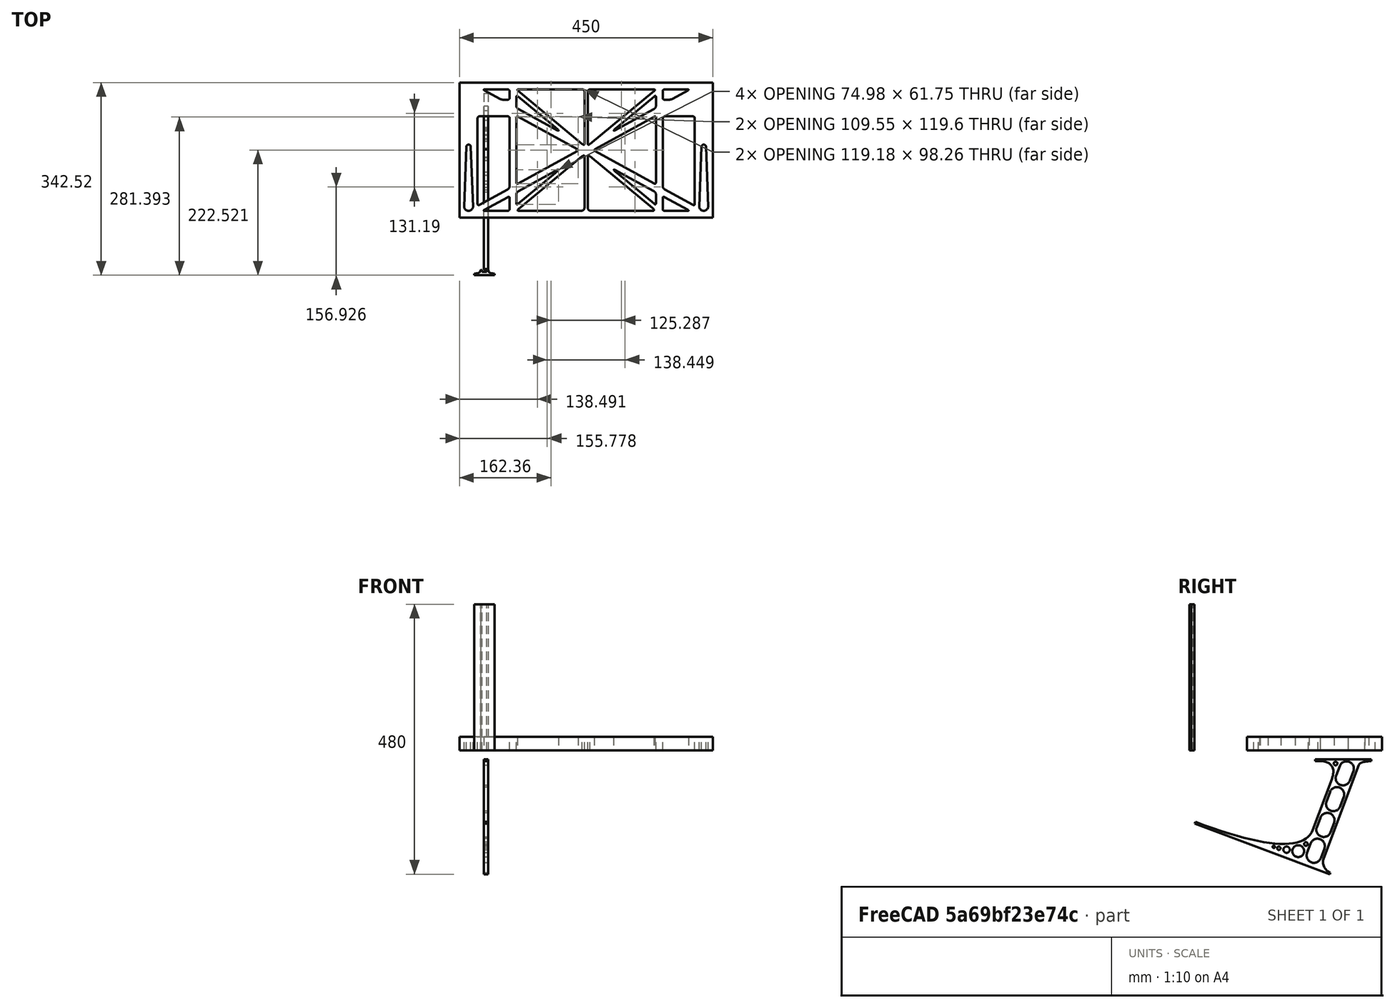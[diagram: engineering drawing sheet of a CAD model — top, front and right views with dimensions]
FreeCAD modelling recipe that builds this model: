
FCSTD DOCUMENT  (FreeCAD 0.19R0.19.2)
Label: laptopStand163FCStd
License: All rights reserved
LicenseURL: http://en.wikipedia.org/wiki/All_rights_reserved
objects: Sketcher::SketchObject×4, Part::Extrusion×3
note: 7 computed .brp shape members not serialized (recipe doc carries the construction recipe); baked Part::Feature solids carry a one-line shape summary decoded from their .brp

FEATURE [Sketcher::SketchObject] Sketch
  FullyConstrained = false
  sketch-geometry (349):
    g0: LineSegment StartX=-10.9272 StartY=-82.7794 StartZ=0 EndX=46.0728 EndY=-51.4823 EndZ=0
    g1: LineSegment StartX=-10.9272 StartY=76.4095 StartZ=0 EndX=-10.9272 EndY=-82.7794 EndZ=0
    g2: LineSegment StartX=46.0728 StartY=76.4095 StartZ=0 EndX=46.0728 EndY=-51.4823 EndZ=0
    g3: LineSegment StartX=-42.9272 StartY=136.221 StartZ=0 EndX=-42.9272 EndY=-103.779 EndZ=0
    g4: LineSegment StartX=407.073 StartY=136.221 StartZ=0 EndX=407.073 EndY=-103.779 EndZ=0
    g5: ArcOfCircle CenterX=-26.9272 CenterY=-83.7794 CenterZ=0 NormalX=0 NormalY=0 NormalZ=1 AngleXU=0 Radius=8 StartAngle=3.14159 EndAngle=6.28319
    g6: ArcOfCircle CenterX=391.073 CenterY=22.1087 CenterZ=0 NormalX=0 NormalY=0 NormalZ=1 AngleXU=0 Radius=8 StartAngle=-4.4e-15 EndAngle=3.14159
    g7: LineSegment StartX=399.073 StartY=22.1087 StartZ=0 EndX=399.073 EndY=-83.7794 EndZ=0
    g8: LineSegment StartX=383.073 StartY=22.1087 StartZ=0 EndX=383.073 EndY=-83.7794 EndZ=0
    g9: ArcOfCircle CenterX=391.073 CenterY=-83.7794 CenterZ=0 NormalX=0 NormalY=0 NormalZ=1 AngleXU=0 Radius=8 StartAngle=3.14159 EndAngle=6.28319
    g10: Circle CenterX=175.022 CenterY=27.0628 CenterZ=0 NormalX=0 NormalY=0 NormalZ=1 AngleXU=0 Radius=1
    g11: Circle CenterX=179.022 CenterY=24.8665 CenterZ=0 NormalX=0 NormalY=0 NormalZ=1 AngleXU=0 Radius=1
    g12: Circle CenterX=179.022 CenterY=27.0628 CenterZ=0 NormalX=0 NormalY=0 NormalZ=1 AngleXU=0 Radius=1
    g13: BSplineCurve PolesCount=3 KnotsCount=2 Degree=2 IsPeriodic=0
    g14: GeomPoint X=175.022 Y=27.0628 Z=0
    g15: GeomPoint X=179.022 Y=27.0628 Z=0
    g16: Circle CenterX=189.124 CenterY=27.0628 CenterZ=0 NormalX=0 NormalY=0 NormalZ=1 AngleXU=0 Radius=1
    g17: Circle CenterX=185.124 CenterY=24.8665 CenterZ=0 NormalX=0 NormalY=0 NormalZ=1 AngleXU=0 Radius=1
    g18: Circle CenterX=185.124 CenterY=27.0628 CenterZ=0 NormalX=0 NormalY=0 NormalZ=1 AngleXU=0 Radius=1
    g19: BSplineCurve PolesCount=3 KnotsCount=2 Degree=2 IsPeriodic=0
    g20: GeomPoint X=189.124 Y=27.0628 Z=0
    g21: GeomPoint X=185.124 Y=27.0628 Z=0
    g22: Circle CenterX=175.022 CenterY=5.37834 CenterZ=0 NormalX=0 NormalY=0 NormalZ=1 AngleXU=0 Radius=1
    g23: Circle CenterX=179.022 CenterY=7.57463 CenterZ=0 NormalX=0 NormalY=0 NormalZ=1 AngleXU=0 Radius=1
    g24: Circle CenterX=179.022 CenterY=5.34704 CenterZ=0 NormalX=0 NormalY=0 NormalZ=1 AngleXU=0 Radius=1
    g25: BSplineCurve PolesCount=3 KnotsCount=2 Degree=2 IsPeriodic=0
    g26: GeomPoint X=175.022 Y=5.37834 Z=0
    g27: GeomPoint X=179.022 Y=5.34704 Z=0
    g28: Circle CenterX=189.124 CenterY=5.37834 CenterZ=0 NormalX=0 NormalY=0 NormalZ=1 AngleXU=0 Radius=1
    g29: Circle CenterX=185.124 CenterY=7.57463 CenterZ=0 NormalX=0 NormalY=0 NormalZ=1 AngleXU=0 Radius=1
    g30: Circle CenterX=185.124 CenterY=5.34704 CenterZ=0 NormalX=0 NormalY=0 NormalZ=1 AngleXU=0 Radius=1
    g31: BSplineCurve PolesCount=3 KnotsCount=2 Degree=2 IsPeriodic=0
    g32: GeomPoint X=189.124 Y=5.37834 Z=0
    g33: GeomPoint X=185.124 Y=5.34704 Z=0
    g34: Circle CenterX=165.871 CenterY=18.1458 CenterZ=0 NormalX=0 NormalY=0 NormalZ=1 AngleXU=0 Radius=1
    g35: Circle CenterX=169.377 CenterY=16.2206 CenterZ=0 NormalX=0 NormalY=0 NormalZ=1 AngleXU=0 Radius=1
    g36: Circle CenterX=165.871 CenterY=14.2954 CenterZ=0 NormalX=0 NormalY=0 NormalZ=1 AngleXU=0 Radius=1
    g37: BSplineCurve PolesCount=3 KnotsCount=2 Degree=2 IsPeriodic=0
    g38: GeomPoint X=165.871 Y=18.1458 Z=0
    g39: GeomPoint X=165.871 Y=14.2954 Z=0
    g40: Circle CenterX=198.275 CenterY=18.1458 CenterZ=0 NormalX=0 NormalY=0 NormalZ=1 AngleXU=0 Radius=1
    g41: Circle CenterX=194.768 CenterY=16.2206 CenterZ=0 NormalX=0 NormalY=0 NormalZ=1 AngleXU=0 Radius=1
    g42: Circle CenterX=198.275 CenterY=14.2954 CenterZ=0 NormalX=0 NormalY=0 NormalZ=1 AngleXU=0 Radius=1
    g43: BSplineCurve PolesCount=3 KnotsCount=2 Degree=2 IsPeriodic=0
    g44: GeomPoint X=198.275 Y=18.1458 Z=0
    g45: GeomPoint X=198.275 Y=14.2954 Z=0
    g46: LineSegment StartX=407.073 StartY=-103.779 StartZ=0 EndX=-42.9272 EndY=-103.779 EndZ=0
    g47: LineSegment StartX=407.073 StartY=136.221 StartZ=0 EndX=-42.9272 EndY=136.221 EndZ=0
    g48: LineSegment StartX=46.0728 StartY=76.4095 StartZ=0 EndX=-10.9272 EndY=76.4095 EndZ=0
    g49: Circle CenterX=125.607 CenterY=54.1951 CenterZ=0 NormalX=0 NormalY=0 NormalZ=1 AngleXU=0 Radius=1
    g50: Circle CenterX=139.632 CenterY=46.4944 CenterZ=0 NormalX=0 NormalY=0 NormalZ=1 AngleXU=0 Radius=1
    g51: Circle CenterX=127.326 CenterY=56.7187 CenterZ=0 NormalX=0 NormalY=0 NormalZ=1 AngleXU=0 Radius=1
    g52: BSplineCurve PolesCount=3 KnotsCount=2 Degree=2 IsPeriodic=0
    g53: GeomPoint X=125.607 Y=54.1951 Z=0
    g54: GeomPoint X=127.326 Y=56.7187 Z=0
    g55: Circle CenterX=236.821 CenterY=56.7187 CenterZ=0 NormalX=0 NormalY=0 NormalZ=1 AngleXU=0 Radius=1
    g56: Circle CenterX=224.513 CenterY=46.4944 CenterZ=0 NormalX=0 NormalY=0 NormalZ=1 AngleXU=0 Radius=1
    g57: Circle CenterX=238.538 CenterY=54.1951 CenterZ=0 NormalX=0 NormalY=0 NormalZ=1 AngleXU=0 Radius=1
    g58: BSplineCurve PolesCount=3 KnotsCount=2 Degree=2 IsPeriodic=0
    g59: GeomPoint X=236.821 Y=56.7187 Z=0
    g60: GeomPoint X=238.538 Y=54.1951 Z=0
    g61: Circle CenterX=238.538 CenterY=-21.7539 CenterZ=0 NormalX=0 NormalY=0 NormalZ=1 AngleXU=0 Radius=1
    g62: Circle CenterX=224.513 CenterY=-14.0532 CenterZ=0 NormalX=0 NormalY=0 NormalZ=1 AngleXU=0 Radius=1
    g63: Circle CenterX=236.821 CenterY=-24.2775 CenterZ=0 NormalX=0 NormalY=0 NormalZ=1 AngleXU=0 Radius=1
    g64: BSplineCurve PolesCount=3 KnotsCount=2 Degree=2 IsPeriodic=0
    g65: GeomPoint X=238.538 Y=-21.7539 Z=0
    g66: GeomPoint X=236.821 Y=-24.2775 Z=0
    g67: Circle CenterX=125.607 CenterY=-21.7539 CenterZ=0 NormalX=0 NormalY=0 NormalZ=1 AngleXU=0 Radius=1
    g68: Circle CenterX=139.632 CenterY=-14.0532 CenterZ=0 NormalX=0 NormalY=0 NormalZ=1 AngleXU=0 Radius=1
    g69: Circle CenterX=127.325 CenterY=-24.2775 CenterZ=0 NormalX=0 NormalY=0 NormalZ=1 AngleXU=0 Radius=1
    g70: BSplineCurve PolesCount=3 KnotsCount=2 Degree=2 IsPeriodic=0
    g71: GeomPoint X=125.607 Y=-21.7539 Z=0
    g72: GeomPoint X=127.325 Y=-24.2775 Z=0
    g73: Circle CenterX=302.996 CenterY=111.695 CenterZ=0 NormalX=0 NormalY=0 NormalZ=1 AngleXU=0 Radius=1
    g74: Circle CenterX=306.073 CenterY=114.251 CenterZ=0 NormalX=0 NormalY=0 NormalZ=1 AngleXU=0 Radius=1
    g75: Circle CenterX=306.073 CenterY=110.251 CenterZ=0 NormalX=0 NormalY=0 NormalZ=1 AngleXU=0 Radius=1
    g76: BSplineCurve PolesCount=3 KnotsCount=2 Degree=2 IsPeriodic=0
    g77: GeomPoint X=302.996 Y=111.695 Z=0
    g78: GeomPoint X=306.073 Y=110.251 Z=0
    g79: Circle CenterX=306.073 CenterY=95.2763 CenterZ=0 NormalX=0 NormalY=0 NormalZ=1 AngleXU=0 Radius=1
    g80: Circle CenterX=306.073 CenterY=91.2763 CenterZ=0 NormalX=0 NormalY=0 NormalZ=1 AngleXU=0 Radius=1
    g81: Circle CenterX=302.567 CenterY=89.3511 CenterZ=0 NormalX=0 NormalY=0 NormalZ=1 AngleXU=0 Radius=1
    g82: BSplineCurve PolesCount=3 KnotsCount=2 Degree=2 IsPeriodic=0
    g83: GeomPoint X=306.073 Y=95.2763 Z=0
    g84: GeomPoint X=302.567 Y=89.3511 Z=0
    g85: LineSegment StartX=306.073 StartY=110.251 StartZ=0 EndX=306.073 EndY=95.2763 EndZ=0
    g86: LineSegment StartX=302.996 StartY=111.695 StartZ=0 EndX=236.821 EndY=56.7187 EndZ=0
    g87: LineSegment StartX=238.538 StartY=54.1951 StartZ=0 EndX=302.567 EndY=89.3511 EndZ=0
    g88: Circle CenterX=61.1496 CenterY=111.695 CenterZ=0 NormalX=0 NormalY=0 NormalZ=1 AngleXU=0 Radius=1
    g89: Circle CenterX=58.0728 CenterY=114.251 CenterZ=0 NormalX=0 NormalY=0 NormalZ=1 AngleXU=0 Radius=1
    g90: Circle CenterX=58.0728 CenterY=110.251 CenterZ=0 NormalX=0 NormalY=0 NormalZ=1 AngleXU=0 Radius=1
    g91: BSplineCurve PolesCount=3 KnotsCount=2 Degree=2 IsPeriodic=0
    g92: GeomPoint X=61.1496 Y=111.695 Z=0
    g93: GeomPoint X=58.0728 Y=110.251 Z=0
    g94: Circle CenterX=61.5791 CenterY=89.3511 CenterZ=0 NormalX=0 NormalY=0 NormalZ=1 AngleXU=0 Radius=1
    g95: Circle CenterX=58.0728 CenterY=91.2763 CenterZ=0 NormalX=0 NormalY=0 NormalZ=1 AngleXU=0 Radius=1
    g96: Circle CenterX=58.0728 CenterY=95.2763 CenterZ=0 NormalX=0 NormalY=0 NormalZ=1 AngleXU=0 Radius=1
    g97: BSplineCurve PolesCount=3 KnotsCount=2 Degree=2 IsPeriodic=0
    g98: GeomPoint X=61.5791 Y=89.3511 Z=0
    g99: GeomPoint X=58.0728 Y=95.2763 Z=0
    g100: LineSegment StartX=58.0728 StartY=110.251 StartZ=0 EndX=58.0728 EndY=95.2763 EndZ=0
    g101: LineSegment StartX=61.1496 StartY=111.695 StartZ=0 EndX=127.326 EndY=56.7187 EndZ=0
    g102: LineSegment StartX=125.607 StartY=54.1951 StartZ=0 EndX=61.5791 EndY=89.3511 EndZ=0
    g103: Circle CenterX=61.5791 CenterY=-56.9099 CenterZ=0 NormalX=0 NormalY=0 NormalZ=1 AngleXU=0 Radius=1
    g104: Circle CenterX=58.0728 CenterY=-58.8351 CenterZ=0 NormalX=0 NormalY=0 NormalZ=1 AngleXU=0 Radius=1
    g105: Circle CenterX=58.0728 CenterY=-62.8351 CenterZ=0 NormalX=0 NormalY=0 NormalZ=1 AngleXU=0 Radius=1
    g106: BSplineCurve PolesCount=3 KnotsCount=2 Degree=2 IsPeriodic=0
    g107: GeomPoint X=61.5791 Y=-56.9099 Z=0
    g108: GeomPoint X=58.0728 Y=-62.8351 Z=0
    g109: Circle CenterX=58.0728 CenterY=-77.8102 CenterZ=0 NormalX=0 NormalY=0 NormalZ=1 AngleXU=0 Radius=1
    g110: Circle CenterX=58.0728 CenterY=-81.8102 CenterZ=0 NormalX=0 NormalY=0 NormalZ=1 AngleXU=0 Radius=1
    g111: Circle CenterX=61.1496 CenterY=-79.2541 CenterZ=0 NormalX=0 NormalY=0 NormalZ=1 AngleXU=0 Radius=1
    g112: BSplineCurve PolesCount=3 KnotsCount=2 Degree=2 IsPeriodic=0
    g113: GeomPoint X=58.0728 Y=-77.8102 Z=0
    g114: GeomPoint X=61.1496 Y=-79.2541 Z=0
    g115: LineSegment StartX=58.0728 StartY=-62.8351 StartZ=0 EndX=58.0728 EndY=-77.8102 EndZ=0
    g116: LineSegment StartX=61.1496 StartY=-79.2541 StartZ=0 EndX=127.325 EndY=-24.2775 EndZ=0
    g117: LineSegment StartX=125.607 StartY=-21.7539 StartZ=0 EndX=61.5791 EndY=-56.9099 EndZ=0
    g118: Circle CenterX=302.567 CenterY=-56.9099 CenterZ=0 NormalX=0 NormalY=0 NormalZ=1 AngleXU=0 Radius=1
    g119: Circle CenterX=306.073 CenterY=-58.8351 CenterZ=0 NormalX=0 NormalY=0 NormalZ=1 AngleXU=0 Radius=1
    g120: Circle CenterX=306.073 CenterY=-62.8351 CenterZ=0 NormalX=0 NormalY=0 NormalZ=1 AngleXU=0 Radius=1
    g121: BSplineCurve PolesCount=3 KnotsCount=2 Degree=2 IsPeriodic=0
    g122: GeomPoint X=302.567 Y=-56.9099 Z=0
    g123: GeomPoint X=306.073 Y=-62.8351 Z=0
    g124: Circle CenterX=302.996 CenterY=-79.2541 CenterZ=0 NormalX=0 NormalY=0 NormalZ=1 AngleXU=0 Radius=1
    g125: Circle CenterX=306.073 CenterY=-81.8102 CenterZ=0 NormalX=0 NormalY=0 NormalZ=1 AngleXU=0 Radius=1
    g126: Circle CenterX=306.073 CenterY=-77.8102 CenterZ=0 NormalX=0 NormalY=0 NormalZ=1 AngleXU=0 Radius=1
    g127: BSplineCurve PolesCount=3 KnotsCount=2 Degree=2 IsPeriodic=0
    g128: GeomPoint X=302.996 Y=-79.2541 Z=0
    g129: GeomPoint X=306.073 Y=-77.8102 Z=0
    g130: LineSegment StartX=306.073 StartY=-62.8351 StartZ=0 EndX=306.073 EndY=-77.8102 EndZ=0
    g131: LineSegment StartX=302.996 StartY=-79.2541 StartZ=0 EndX=236.821 EndY=-24.2775 EndZ=0
    g132: LineSegment StartX=238.538 StartY=-21.7539 StartZ=0 EndX=302.567 EndY=-56.9099 EndZ=0
    g133: Circle CenterX=61.6457 CenterY=-88.8112 CenterZ=0 NormalX=0 NormalY=0 NormalZ=1 AngleXU=0 Radius=1
    g134: Circle CenterX=58.0728 CenterY=-91.7794 CenterZ=0 NormalX=0 NormalY=0 NormalZ=1 AngleXU=0 Radius=1
    g135: Circle CenterX=63.9135 CenterY=-91.7794 CenterZ=0 NormalX=0 NormalY=0 NormalZ=1 AngleXU=0 Radius=1
    g136: BSplineCurve PolesCount=3 KnotsCount=2 Degree=2 IsPeriodic=0
    g137: GeomPoint X=61.6457 Y=-88.8112 Z=0
    g138: GeomPoint X=63.9135 Y=-91.7794 Z=0
    g139: Circle CenterX=179.022 CenterY=-85.8163 CenterZ=0 NormalX=0 NormalY=0 NormalZ=1 AngleXU=0 Radius=1
    g140: Circle CenterX=179.022 CenterY=-91.7794 CenterZ=0 NormalX=0 NormalY=0 NormalZ=1 AngleXU=0 Radius=1
    g141: Circle CenterX=171.895 CenterY=-91.7794 CenterZ=0 NormalX=0 NormalY=0 NormalZ=1 AngleXU=0 Radius=1
    g142: BSplineCurve PolesCount=3 KnotsCount=2 Degree=2 IsPeriodic=0
    g143: GeomPoint X=179.022 Y=-85.8163 Z=0
    g144: GeomPoint X=171.895 Y=-91.7794 Z=0
    g145: Circle CenterX=185.124 CenterY=-86.2028 CenterZ=0 NormalX=0 NormalY=0 NormalZ=1 AngleXU=0 Radius=1
    g146: Circle CenterX=185.124 CenterY=-91.7794 CenterZ=0 NormalX=0 NormalY=0 NormalZ=1 AngleXU=0 Radius=1
    g147: Circle CenterX=191.747 CenterY=-91.7794 CenterZ=0 NormalX=0 NormalY=0 NormalZ=1 AngleXU=0 Radius=1
    g148: BSplineCurve PolesCount=3 KnotsCount=2 Degree=2 IsPeriodic=0
    g149: GeomPoint X=185.124 Y=-86.2028 Z=0
    g150: GeomPoint X=191.747 Y=-91.7794 Z=0
    g151: Circle CenterX=299.888 CenterY=-86.6413 CenterZ=0 NormalX=0 NormalY=0 NormalZ=1 AngleXU=0 Radius=1
    g152: Circle CenterX=306.073 CenterY=-91.7794 CenterZ=0 NormalX=0 NormalY=0 NormalZ=1 AngleXU=0 Radius=1
    g153: Circle CenterX=298.776 CenterY=-91.7794 CenterZ=0 NormalX=0 NormalY=0 NormalZ=1 AngleXU=0 Radius=1
    g154: BSplineCurve PolesCount=3 KnotsCount=2 Degree=2 IsPeriodic=0
    g155: GeomPoint X=299.888 Y=-86.6413 Z=0
    g156: GeomPoint X=298.776 Y=-91.7794 Z=0
    g157: LineSegment StartX=189.124 StartY=5.37834 StartZ=0 EndX=299.888 EndY=-86.6413 EndZ=0
    g158: LineSegment StartX=298.776 StartY=-91.7794 StartZ=0 EndX=191.747 EndY=-91.7794 EndZ=0
    g159: LineSegment StartX=185.124 StartY=-86.2028 StartZ=0 EndX=185.124 EndY=5.34704 EndZ=0
    g160: LineSegment StartX=179.022 StartY=5.34704 StartZ=0 EndX=179.022 EndY=-85.8163 EndZ=0
    g161: LineSegment StartX=171.895 StartY=-91.7794 StartZ=0 EndX=63.9135 EndY=-91.7794 EndZ=0
    g162: LineSegment StartX=61.6457 StartY=-88.8112 StartZ=0 EndX=175.022 EndY=5.37834 EndZ=0
    g163: Circle CenterX=302.073 CenterY=124.221 CenterZ=0 NormalX=0 NormalY=0 NormalZ=1 AngleXU=0 Radius=1
    g164: Circle CenterX=306.073 CenterY=124.221 CenterZ=0 NormalX=0 NormalY=0 NormalZ=1 AngleXU=0 Radius=1
    g165: Circle CenterX=302.996 CenterY=121.665 CenterZ=0 NormalX=0 NormalY=0 NormalZ=1 AngleXU=0 Radius=1
    g166: BSplineCurve PolesCount=3 KnotsCount=2 Degree=2 IsPeriodic=0
    g167: GeomPoint X=302.073 Y=124.221 Z=0
    g168: GeomPoint X=302.996 Y=121.665 Z=0
    g169: Circle CenterX=189.124 CenterY=124.221 CenterZ=0 NormalX=0 NormalY=0 NormalZ=1 AngleXU=0 Radius=1
    g170: Circle CenterX=185.124 CenterY=124.221 CenterZ=0 NormalX=0 NormalY=0 NormalZ=1 AngleXU=0 Radius=1
    g171: Circle CenterX=185.124 CenterY=120.221 CenterZ=0 NormalX=0 NormalY=0 NormalZ=1 AngleXU=0 Radius=1
    g172: BSplineCurve PolesCount=3 KnotsCount=2 Degree=2 IsPeriodic=0
    g173: GeomPoint X=189.124 Y=124.221 Z=0
    g174: GeomPoint X=185.124 Y=120.221 Z=0
    g175: Circle CenterX=175.022 CenterY=124.221 CenterZ=0 NormalX=0 NormalY=0 NormalZ=1 AngleXU=0 Radius=1
    g176: Circle CenterX=179.022 CenterY=124.221 CenterZ=0 NormalX=0 NormalY=0 NormalZ=1 AngleXU=0 Radius=1
    g177: Circle CenterX=179.022 CenterY=120.221 CenterZ=0 NormalX=0 NormalY=0 NormalZ=1 AngleXU=0 Radius=1
    g178: BSplineCurve PolesCount=3 KnotsCount=2 Degree=2 IsPeriodic=0
    g179: GeomPoint X=175.022 Y=124.221 Z=0
    g180: GeomPoint X=179.022 Y=120.221 Z=0
    g181: Circle CenterX=62.0728 CenterY=124.221 CenterZ=0 NormalX=0 NormalY=0 NormalZ=1 AngleXU=0 Radius=1
    g182: Circle CenterX=58.0728 CenterY=124.221 CenterZ=0 NormalX=0 NormalY=0 NormalZ=1 AngleXU=0 Radius=1
    g183: Circle CenterX=61.1496 CenterY=121.665 CenterZ=0 NormalX=0 NormalY=0 NormalZ=1 AngleXU=0 Radius=1
    g184: BSplineCurve PolesCount=3 KnotsCount=2 Degree=2 IsPeriodic=0
    g185: GeomPoint X=62.0728 Y=124.221 Z=0
    g186: GeomPoint X=61.1496 Y=121.665 Z=0
    g187: LineSegment StartX=62.0728 StartY=124.221 StartZ=0 EndX=175.022 EndY=124.221 EndZ=0
    g188: LineSegment StartX=179.022 StartY=120.221 StartZ=0 EndX=179.022 EndY=27.0628 EndZ=0
    g189: LineSegment StartX=185.124 StartY=27.0628 StartZ=0 EndX=185.124 EndY=120.221 EndZ=0
    g190: LineSegment StartX=189.124 StartY=124.221 StartZ=0 EndX=302.073 EndY=124.221 EndZ=0
    g191: LineSegment StartX=302.996 StartY=121.665 StartZ=0 EndX=189.124 EndY=27.0628 EndZ=0
    g192: LineSegment StartX=175.022 StartY=27.0628 StartZ=0 EndX=61.1496 EndY=121.665 EndZ=0
    g193: Circle CenterX=61.5791 CenterY=75.4095 CenterZ=0 NormalX=0 NormalY=0 NormalZ=1 AngleXU=0 Radius=1
    g194: Circle CenterX=58.0728 CenterY=77.3346 CenterZ=0 NormalX=0 NormalY=0 NormalZ=1 AngleXU=0 Radius=1
    g195: Circle CenterX=58.0728 CenterY=73.3346 CenterZ=0 NormalX=0 NormalY=0 NormalZ=1 AngleXU=0 Radius=1
    g196: BSplineCurve PolesCount=3 KnotsCount=2 Degree=2 IsPeriodic=0
    g197: GeomPoint X=61.5791 Y=75.4095 Z=0
    g198: GeomPoint X=58.0728 Y=73.3346 Z=0
    g199: Circle CenterX=58.0728 CenterY=-40.8935 CenterZ=0 NormalX=0 NormalY=0 NormalZ=1 AngleXU=0 Radius=1
    g200: Circle CenterX=58.0728 CenterY=-44.8935 CenterZ=0 NormalX=0 NormalY=0 NormalZ=1 AngleXU=0 Radius=1
    g201: Circle CenterX=61.5791 CenterY=-42.9683 CenterZ=0 NormalX=0 NormalY=0 NormalZ=1 AngleXU=0 Radius=1
    g202: BSplineCurve PolesCount=3 KnotsCount=2 Degree=2 IsPeriodic=0
    g203: GeomPoint X=58.0728 Y=-40.8935 Z=0
    g204: GeomPoint X=61.5791 Y=-42.9683 Z=0
    g205: LineSegment StartX=61.5791 StartY=-42.9683 StartZ=0 EndX=165.871 EndY=14.2954 EndZ=0
    g206: LineSegment StartX=165.871 StartY=18.1458 StartZ=0 EndX=61.5791 EndY=75.4095 EndZ=0
    g207: LineSegment StartX=58.0728 StartY=73.3346 StartZ=0 EndX=58.0728 EndY=-40.8935 EndZ=0
    g208: Circle CenterX=302.567 CenterY=-42.9683 CenterZ=0 NormalX=0 NormalY=0 NormalZ=1 AngleXU=0 Radius=1
    g209: Circle CenterX=306.073 CenterY=-44.8935 CenterZ=0 NormalX=0 NormalY=0 NormalZ=1 AngleXU=0 Radius=1
    g210: Circle CenterX=306.073 CenterY=-40.8935 CenterZ=0 NormalX=0 NormalY=0 NormalZ=1 AngleXU=0 Radius=1
    g211: BSplineCurve PolesCount=3 KnotsCount=2 Degree=2 IsPeriodic=0
    g212: GeomPoint X=302.567 Y=-42.9683 Z=0
    g213: GeomPoint X=306.073 Y=-40.8935 Z=0
    g214: Circle CenterX=306.073 CenterY=73.3346 CenterZ=0 NormalX=0 NormalY=0 NormalZ=1 AngleXU=0 Radius=1
    g215: Circle CenterX=306.073 CenterY=77.3346 CenterZ=0 NormalX=0 NormalY=0 NormalZ=1 AngleXU=0 Radius=1
    g216: Circle CenterX=302.567 CenterY=75.4095 CenterZ=0 NormalX=0 NormalY=0 NormalZ=1 AngleXU=0 Radius=1
    g217: BSplineCurve PolesCount=3 KnotsCount=2 Degree=2 IsPeriodic=0
    g218: GeomPoint X=306.073 Y=73.3346 Z=0
    g219: GeomPoint X=302.567 Y=75.4095 Z=0
    g220: LineSegment StartX=302.567 StartY=-42.9683 StartZ=0 EndX=198.275 EndY=14.2954 EndZ=0
    g221: LineSegment StartX=198.275 StartY=18.1458 StartZ=0 EndX=302.567 EndY=75.4095 EndZ=0
    g222: LineSegment StartX=306.073 StartY=73.3346 StartZ=0 EndX=306.073 EndY=-40.8935 EndZ=0
    g223: LineSegment StartX=322.073 StartY=105.865 StartZ=0 EndX=328.643 EndY=105.865 EndZ=0
    g224: LineSegment StartX=318.073 StartY=120.221 StartZ=0 EndX=318.073 EndY=109.865 EndZ=0
    g225: LineSegment StartX=336.157 StartY=107.779 StartZ=0 EndX=362.567 EndY=122.294 EndZ=0
    g226: Circle CenterX=362.073 CenterY=124.221 CenterZ=0 NormalX=0 NormalY=0 NormalZ=1 AngleXU=0 Radius=1
    g227: Circle CenterX=366.073 CenterY=124.221 CenterZ=0 NormalX=0 NormalY=0 NormalZ=1 AngleXU=0 Radius=1
    g228: Circle CenterX=362.567 CenterY=122.294 CenterZ=0 NormalX=0 NormalY=0 NormalZ=1 AngleXU=0 Radius=1
    g229: BSplineCurve PolesCount=3 KnotsCount=2 Degree=2 IsPeriodic=0
    g230: GeomPoint X=362.073 Y=124.221 Z=0
    g231: GeomPoint X=362.567 Y=122.294 Z=0
    g232: Circle CenterX=322.073 CenterY=124.221 CenterZ=0 NormalX=0 NormalY=0 NormalZ=1 AngleXU=0 Radius=1
    g233: Circle CenterX=318.073 CenterY=124.221 CenterZ=0 NormalX=0 NormalY=0 NormalZ=1 AngleXU=0 Radius=1
    g234: Circle CenterX=318.073 CenterY=120.221 CenterZ=0 NormalX=0 NormalY=0 NormalZ=1 AngleXU=0 Radius=1
    g235: BSplineCurve PolesCount=3 KnotsCount=2 Degree=2 IsPeriodic=0
    g236: GeomPoint X=322.073 Y=124.221 Z=0
    g237: GeomPoint X=318.073 Y=120.221 Z=0
    g238: Circle CenterX=322.073 CenterY=105.865 CenterZ=0 NormalX=0 NormalY=0 NormalZ=1 AngleXU=0 Radius=1
    g239: Circle CenterX=318.073 CenterY=105.865 CenterZ=0 NormalX=0 NormalY=0 NormalZ=1 AngleXU=0 Radius=1
    g240: Circle CenterX=318.073 CenterY=109.865 CenterZ=0 NormalX=0 NormalY=0 NormalZ=1 AngleXU=0 Radius=1
    g241: BSplineCurve PolesCount=3 KnotsCount=2 Degree=2 IsPeriodic=0
    g242: GeomPoint X=322.073 Y=105.865 Z=0
    g243: GeomPoint X=318.073 Y=109.865 Z=0
    g244: Circle CenterX=336.157 CenterY=107.779 CenterZ=0 NormalX=0 NormalY=0 NormalZ=1 AngleXU=0 Radius=1
    g245: Circle CenterX=332.651 CenterY=105.853 CenterZ=0 NormalX=0 NormalY=0 NormalZ=1 AngleXU=0 Radius=1
    g246: Circle CenterX=328.643 CenterY=105.865 CenterZ=0 NormalX=0 NormalY=0 NormalZ=1 AngleXU=0 Radius=1
    g247: BSplineCurve PolesCount=3 KnotsCount=2 Degree=2 IsPeriodic=0
    g248: GeomPoint X=336.157 Y=107.779 Z=0
    g249: GeomPoint X=328.643 Y=105.865 Z=0
    g250: LineSegment StartX=322.073 StartY=124.221 StartZ=0 EndX=362.073 EndY=124.221 EndZ=0
    g251: Circle CenterX=371.567 CenterY=-80.8644 CenterZ=0 NormalX=0 NormalY=0 NormalZ=1 AngleXU=0 Radius=1
    g252: Circle CenterX=375.073 CenterY=-82.7896 CenterZ=0 NormalX=0 NormalY=0 NormalZ=1 AngleXU=0 Radius=1
    g253: Circle CenterX=375.073 CenterY=-78.7896 CenterZ=0 NormalX=0 NormalY=0 NormalZ=1 AngleXU=0 Radius=1
    g254: BSplineCurve PolesCount=3 KnotsCount=2 Degree=2 IsPeriodic=0
    g255: GeomPoint X=371.567 Y=-80.8644 Z=0
    g256: GeomPoint X=375.073 Y=-78.7896 Z=0
    g257: Circle CenterX=321.579 CenterY=-53.4075 CenterZ=0 NormalX=0 NormalY=0 NormalZ=1 AngleXU=0 Radius=1
    g258: Circle CenterX=318.073 CenterY=-51.4823 CenterZ=0 NormalX=0 NormalY=0 NormalZ=1 AngleXU=0 Radius=1
    g259: Circle CenterX=318.073 CenterY=-47.4805 CenterZ=0 NormalX=0 NormalY=0 NormalZ=1 AngleXU=0 Radius=1
    g260: BSplineCurve PolesCount=3 KnotsCount=2 Degree=2 IsPeriodic=0
    g261: GeomPoint X=321.579 Y=-53.4075 Z=0
    g262: GeomPoint X=318.073 Y=-47.4805 Z=0
    g263: LineSegment StartX=371.567 StartY=-80.8644 StartZ=0 EndX=321.579 EndY=-53.4075 EndZ=0
    g264: Circle CenterX=321.579 CenterY=-67.3492 CenterZ=0 NormalX=0 NormalY=0 NormalZ=1 AngleXU=0 Radius=1
    g265: Circle CenterX=318.073 CenterY=-65.424 CenterZ=0 NormalX=0 NormalY=0 NormalZ=1 AngleXU=0 Radius=1
    g266: Circle CenterX=318.073 CenterY=-69.424 CenterZ=0 NormalX=0 NormalY=0 NormalZ=1 AngleXU=0 Radius=1
    g267: BSplineCurve PolesCount=3 KnotsCount=2 Degree=2 IsPeriodic=0
    g268: GeomPoint X=321.579 Y=-67.3492 Z=0
    g269: GeomPoint X=318.073 Y=-69.424 Z=0
    g270: Circle CenterX=362.567 CenterY=-89.8542 CenterZ=0 NormalX=0 NormalY=0 NormalZ=1 AngleXU=0 Radius=1
    g271: Circle CenterX=366.073 CenterY=-91.7794 CenterZ=0 NormalX=0 NormalY=0 NormalZ=1 AngleXU=0 Radius=1
    g272: Circle CenterX=362.073 CenterY=-91.7794 CenterZ=0 NormalX=0 NormalY=0 NormalZ=1 AngleXU=0 Radius=1
    g273: BSplineCurve PolesCount=3 KnotsCount=2 Degree=2 IsPeriodic=0
    g274: GeomPoint X=362.567 Y=-89.8542 Z=0
    g275: GeomPoint X=362.073 Y=-91.7794 Z=0
    g276: Circle CenterX=322.073 CenterY=-91.7794 CenterZ=0 NormalX=0 NormalY=0 NormalZ=1 AngleXU=0 Radius=1
    g277: Circle CenterX=318.073 CenterY=-91.7794 CenterZ=0 NormalX=0 NormalY=0 NormalZ=1 AngleXU=0 Radius=1
    g278: Circle CenterX=318.073 CenterY=-87.7794 CenterZ=0 NormalX=0 NormalY=0 NormalZ=1 AngleXU=0 Radius=1
    g279: BSplineCurve PolesCount=3 KnotsCount=2 Degree=2 IsPeriodic=0
    g280: GeomPoint X=322.073 Y=-91.7794 Z=0
    g281: GeomPoint X=318.073 Y=-87.7794 Z=0
    g282: LineSegment StartX=362.567 StartY=-89.8542 StartZ=0 EndX=321.579 EndY=-67.3492 EndZ=0
    g283: LineSegment StartX=318.073 StartY=-69.424 StartZ=0 EndX=318.073 EndY=-87.7794 EndZ=0
    g284: LineSegment StartX=322.073 StartY=-91.7794 StartZ=0 EndX=362.073 EndY=-91.7794 EndZ=0
    g285: Circle CenterX=2.07281 CenterY=124.221 CenterZ=0 NormalX=0 NormalY=0 NormalZ=1 AngleXU=0 Radius=1
    g286: Circle CenterX=1.57905 CenterY=122.295 CenterZ=0 NormalX=0 NormalY=0 NormalZ=1 AngleXU=0 Radius=1
    g287: BSplineCurve PolesCount=3 KnotsCount=2 Degree=2 IsPeriodic=0
    g288: GeomPoint X=2.07281 Y=124.221 Z=0
    g289: GeomPoint X=1.57905 Y=122.295 Z=0
    g290: Circle CenterX=42.0728 CenterY=124.221 CenterZ=0 NormalX=0 NormalY=0 NormalZ=1 AngleXU=0 Radius=1
    g291: Circle CenterX=46.0728 CenterY=124.221 CenterZ=0 NormalX=0 NormalY=0 NormalZ=1 AngleXU=0 Radius=1
    g292: Circle CenterX=46.0728 CenterY=120.221 CenterZ=0 NormalX=0 NormalY=0 NormalZ=1 AngleXU=0 Radius=1
    g293: BSplineCurve PolesCount=3 KnotsCount=2 Degree=2 IsPeriodic=0
    g294: GeomPoint X=42.0728 Y=124.221 Z=0
    g295: GeomPoint X=46.0728 Y=120.221 Z=0
    g296: Circle CenterX=46.0728 CenterY=109.865 CenterZ=0 NormalX=0 NormalY=0 NormalZ=1 AngleXU=0 Radius=1
    g297: Circle CenterX=46.0728 CenterY=105.865 CenterZ=0 NormalX=0 NormalY=0 NormalZ=1 AngleXU=0 Radius=1
    g298: Circle CenterX=42.0728 CenterY=105.865 CenterZ=0 NormalX=0 NormalY=0 NormalZ=1 AngleXU=0 Radius=1
    g299: BSplineCurve PolesCount=3 KnotsCount=2 Degree=2 IsPeriodic=0
    g300: GeomPoint X=46.0728 Y=109.865 Z=0
    g301: GeomPoint X=42.0728 Y=105.865 Z=0
    g302: Circle CenterX=35.5028 CenterY=105.865 CenterZ=0 NormalX=0 NormalY=0 NormalZ=1 AngleXU=0 Radius=1
    g303: Circle CenterX=31.5028 CenterY=105.865 CenterZ=0 NormalX=0 NormalY=0 NormalZ=1 AngleXU=0 Radius=1
    g304: Circle CenterX=27.9965 CenterY=107.79 CenterZ=0 NormalX=0 NormalY=0 NormalZ=1 AngleXU=0 Radius=1
    g305: BSplineCurve PolesCount=3 KnotsCount=2 Degree=2 IsPeriodic=0
    g306: GeomPoint X=35.5028 Y=105.865 Z=0
    g307: GeomPoint X=27.9965 Y=107.79 Z=0
    g308: LineSegment StartX=2.07281 StartY=124.221 StartZ=0 EndX=42.0728 EndY=124.221 EndZ=0
    g309: LineSegment StartX=46.0728 StartY=120.221 StartZ=0 EndX=46.0728 EndY=109.865 EndZ=0
    g310: LineSegment StartX=42.0728 StartY=105.865 StartZ=0 EndX=35.5028 EndY=105.865 EndZ=0
    g311: LineSegment StartX=27.9965 StartY=107.79 StartZ=0 EndX=1.57905 EndY=122.295 EndZ=0
    g312: Circle CenterX=42.5666 CenterY=-67.3492 CenterZ=0 NormalX=0 NormalY=0 NormalZ=1 AngleXU=0 Radius=1
    g313: Circle CenterX=46.0728 CenterY=-65.424 CenterZ=0 NormalX=0 NormalY=0 NormalZ=1 AngleXU=0 Radius=1
    g314: Circle CenterX=46.0728 CenterY=-69.424 CenterZ=0 NormalX=0 NormalY=0 NormalZ=1 AngleXU=0 Radius=1
    g315: BSplineCurve PolesCount=3 KnotsCount=2 Degree=2 IsPeriodic=0
    g316: GeomPoint X=42.5666 Y=-67.3492 Z=0
    g317: GeomPoint X=46.0728 Y=-69.424 Z=0
    g318: Circle CenterX=46.0728 CenterY=-87.7794 CenterZ=0 NormalX=0 NormalY=0 NormalZ=1 AngleXU=0 Radius=1
    g319: Circle CenterX=46.0728 CenterY=-91.7794 CenterZ=0 NormalX=0 NormalY=0 NormalZ=1 AngleXU=0 Radius=1
    g320: Circle CenterX=42.0728 CenterY=-91.7794 CenterZ=0 NormalX=0 NormalY=0 NormalZ=1 AngleXU=0 Radius=1
    g321: BSplineCurve PolesCount=3 KnotsCount=2 Degree=2 IsPeriodic=0
    g322: GeomPoint X=46.0728 Y=-87.7794 Z=0
    g323: GeomPoint X=42.0728 Y=-91.7794 Z=0
    g324: Circle CenterX=2.07281 CenterY=-91.7794 CenterZ=0 NormalX=0 NormalY=0 NormalZ=1 AngleXU=0 Radius=1
    g325: Circle CenterX=-1.92719 CenterY=-91.7794 CenterZ=0 NormalX=0 NormalY=0 NormalZ=1 AngleXU=0 Radius=1
    g326: Circle CenterX=1.57905 CenterY=-89.8542 CenterZ=0 NormalX=0 NormalY=0 NormalZ=1 AngleXU=0 Radius=1
    g327: BSplineCurve PolesCount=3 KnotsCount=2 Degree=2 IsPeriodic=0
    g328: GeomPoint X=2.07281 Y=-91.7794 Z=0
    g329: GeomPoint X=1.57905 Y=-89.8542 Z=0
    g330: LineSegment StartX=2.07281 StartY=-91.7794 StartZ=0 EndX=42.0728 EndY=-91.7794 EndZ=0
    g331: LineSegment StartX=46.0728 StartY=-87.7794 StartZ=0 EndX=46.0728 EndY=-69.424 EndZ=0
    g332: LineSegment StartX=42.5666 StartY=-67.3492 StartZ=0 EndX=1.57905 EndY=-89.8542 EndZ=0
    g333: Circle CenterX=322.073 CenterY=76.4095 CenterZ=0 NormalX=0 NormalY=0 NormalZ=1 AngleXU=0 Radius=4
    g334: BSplineCurve PolesCount=3 KnotsCount=2 Degree=2 IsPeriodic=0
    g335: GeomPoint X=318.073 Y=72.4095 Z=0
    g336: GeomPoint X=322.073 Y=76.4095 Z=0
    g337: Circle CenterX=375.073 CenterY=72.4095 CenterZ=0 NormalX=0 NormalY=0 NormalZ=1 AngleXU=0 Radius=1
    g338: Circle CenterX=375.073 CenterY=76.4095 CenterZ=0 NormalX=0 NormalY=0 NormalZ=1 AngleXU=0 Radius=1
    g339: Circle CenterX=371.073 CenterY=76.4095 CenterZ=0 NormalX=0 NormalY=0 NormalZ=1 AngleXU=0 Radius=1
    g340: BSplineCurve PolesCount=3 KnotsCount=2 Degree=2 IsPeriodic=0
    g341: GeomPoint X=375.073 Y=72.4095 Z=0
    g342: GeomPoint X=371.073 Y=76.4095 Z=0
    g343: LineSegment StartX=322.073 StartY=76.4095 StartZ=0 EndX=371.073 EndY=76.4095 EndZ=0
    g344: LineSegment StartX=318.073 StartY=72.4095 StartZ=0 EndX=318.073 EndY=-47.4805 EndZ=0
    g345: LineSegment StartX=375.073 StartY=72.4095 StartZ=0 EndX=375.073 EndY=-78.7896 EndZ=0
    g346: ArcOfCircle CenterX=-26.9272 CenterY=22.1087 CenterZ=0 NormalX=0 NormalY=0 NormalZ=1 AngleXU=0 Radius=4 StartAngle=5e-16 EndAngle=3.14159
    g347: LineSegment StartX=-30.9272 StartY=22.1087 StartZ=0 EndX=-34.9272 EndY=-83.7794 EndZ=0
    g348: LineSegment StartX=-18.9272 StartY=-83.7794 StartZ=0 EndX=-22.9272 EndY=22.1087 EndZ=0
  constraints (572):
    c: Coincident(g0,g2)
    c: Block(g0)
    c: Block(g1)
    c: Vertical(g3)
    c: Vertical(g4)
    c: Block(g4)
    c: Block(g3)
    c: Tangent(g6,g7) = 1.5708
    c: Tangent(g7,g9) = 1.5708
    c: Equal(g6,g9)
    c: Coincident(g8,g6)
    c: Coincident(g8,g9)
    c: Block(g7)
    c: Block(g8)
    c: Weight(g10) = 1
    c: Equal(g10,g11)
    c: Equal(g10,g12)
    c: InternalAlignment(g10,g13)
    c: InternalAlignment(g11,g13)
    c: InternalAlignment(g12,g13)
    c: InternalAlignment(g14,g13)
    c: InternalAlignment(g15,g13)
    c: Weight(g16) = 1
    c: Equal(g16,g17)
    c: Equal(g16,g18)
    c: InternalAlignment(g16,g19)
    c: InternalAlignment(g17,g19)
    c: InternalAlignment(g18,g19)
    c: InternalAlignment(g20,g19)
    c: InternalAlignment(g21,g19)
    c: Block(g19)
    c: Block(g13)
    c: Weight(g22) = 1
    c: Equal(g22,g23)
    c: Equal(g22,g24)
    c: InternalAlignment(g22,g25)
    c: InternalAlignment(g23,g25)
    c: InternalAlignment(g24,g25)
    c: InternalAlignment(g26,g25)
    c: InternalAlignment(g27,g25)
    c: Weight(g28) = 1
    c: Equal(g28,g29)
    c: Equal(g28,g30)
    c: InternalAlignment(g28,g31)
    c: InternalAlignment(g29,g31)
    c: InternalAlignment(g30,g31)
    c: InternalAlignment(g32,g31)
    c: InternalAlignment(g33,g31)
    c: Block(g31)
    c: Block(g25)
    c: Weight(g34) = 1
    c: Equal(g34,g35)
    c: Equal(g34,g36)
    c: InternalAlignment(g34,g37)
    c: InternalAlignment(g35,g37)
    c: InternalAlignment(g36,g37)
    c: InternalAlignment(g38,g37)
    c: InternalAlignment(g39,g37)
    c: Weight(g40) = 1
    c: Equal(g40,g41)
    c: Equal(g40,g42)
    c: InternalAlignment(g40,g43)
    c: InternalAlignment(g41,g43)
    c: InternalAlignment(g42,g43)
    c: InternalAlignment(g44,g43)
    c: InternalAlignment(g45,g43)
    c: Block(g37)
    c: Block(g43)
    c: Coincident(g46,g4)
    c: Coincident(g46,g3)
    c: Horizontal(g46)
    c: Distance(g46) = 450
    c: Coincident(g47,g4)
    c: Coincident(g47,g3)
    c: Horizontal(g47)
    c: Horizontal(g48)
    c: Coincident(g2,g48)
    c: Block(g48)
    c: Coincident(g1,g48)
    c: Weight(g49) = 1
    c: Equal(g49,g50)
    c: Equal(g49,g51)
    c: InternalAlignment(g49,g52)
    c: InternalAlignment(g50,g52)
    c: InternalAlignment(g51,g52)
    c: InternalAlignment(g53,g52)
    c: InternalAlignment(g54,g52)
    c: Block(g52)
    c: Weight(g55) = 1
    c: Equal(g55,g56)
    c: Equal(g55,g57)
    c: InternalAlignment(g55,g58)
    c: InternalAlignment(g56,g58)
    c: InternalAlignment(g57,g58)
    c: InternalAlignment(g59,g58)
    c: InternalAlignment(g60,g58)
    c: Block(g58)
    c: Weight(g61) = 1
    c: Equal(g61,g62)
    c: Equal(g61,g63)
    c: InternalAlignment(g61,g64)
    c: InternalAlignment(g62,g64)
    c: InternalAlignment(g63,g64)
    c: InternalAlignment(g65,g64)
    c: InternalAlignment(g66,g64)
    c: Block(g64)
    c: Weight(g67) = 1
    c: Equal(g67,g68)
    c: Equal(g67,g69)
    c: InternalAlignment(g67,g70)
    c: InternalAlignment(g68,g70)
    c: InternalAlignment(g69,g70)
    c: InternalAlignment(g71,g70)
    c: InternalAlignment(g72,g70)
    c: Block(g70)
    c: Weight(g73) = 1
    c: Equal(g73,g74)
    c: Equal(g73,g75)
    c: InternalAlignment(g73,g76)
    c: InternalAlignment(g74,g76)
    c: InternalAlignment(g75,g76)
    c: InternalAlignment(g77,g76)
    c: InternalAlignment(g78,g76)
    c: Weight(g79) = 1
    c: Equal(g79,g80)
    c: Equal(g79,g81)
    c: InternalAlignment(g79,g82)
    c: InternalAlignment(g80,g82)
    c: InternalAlignment(g81,g82)
    c: InternalAlignment(g83,g82)
    c: InternalAlignment(g84,g82)
    c: Block(g76)
    c: Block(g82)
    c: Coincident(g85,g76)
    c: Coincident(g85,g82)
    c: Vertical(g85)
    c: Coincident(g86,g76)
    c: Coincident(g86,g58)
    c: Coincident(g87,g58)
    c: Coincident(g87,g82)
    c: Weight(g88) = 1
    c: Equal(g88,g89)
    c: Equal(g88,g90)
    c: InternalAlignment(g88,g91)
    c: InternalAlignment(g89,g91)
    c: InternalAlignment(g90,g91)
    c: InternalAlignment(g92,g91)
    c: InternalAlignment(g93,g91)
    c: Weight(g94) = 1
    c: Equal(g94,g95)
    c: Equal(g94,g96)
    c: InternalAlignment(g94,g97)
    c: InternalAlignment(g95,g97)
    c: InternalAlignment(g96,g97)
    c: InternalAlignment(g98,g97)
    c: InternalAlignment(g99,g97)
    c: Block(g91)
    c: Block(g97)
    c: Coincident(g100,g91)
    c: Coincident(g100,g97)
    c: Vertical(g100)
    c: Coincident(g101,g91)
    c: Coincident(g101,g52)
    c: Coincident(g102,g52)
    c: Coincident(g102,g97)
    c: Weight(g103) = 1
    c: Equal(g103,g104)
    c: Equal(g103,g105)
    c: InternalAlignment(g103,g106)
    c: InternalAlignment(g104,g106)
    c: InternalAlignment(g105,g106)
    c: InternalAlignment(g107,g106)
    c: InternalAlignment(g108,g106)
    c: Weight(g109) = 1
    c: Equal(g109,g110)
    c: Equal(g109,g111)
    c: InternalAlignment(g109,g112)
    c: InternalAlignment(g110,g112)
    c: InternalAlignment(g111,g112)
    c: InternalAlignment(g113,g112)
    c: InternalAlignment(g114,g112)
    c: Block(g106)
    c: Block(g112)
    c: Coincident(g115,g106)
    c: Coincident(g115,g112)
    c: Vertical(g115)
    c: Coincident(g116,g112)
    c: Coincident(g116,g70)
    c: Coincident(g117,g70)
    c: Coincident(g117,g106)
    c: Weight(g118) = 1
    c: Equal(g118,g119)
    c: Equal(g118,g120)
    c: InternalAlignment(g118,g121)
    c: InternalAlignment(g119,g121)
    c: InternalAlignment(g120,g121)
    c: InternalAlignment(g122,g121)
    c: InternalAlignment(g123,g121)
    c: Weight(g124) = 1
    c: Equal(g124,g125)
    c: Equal(g124,g126)
    c: InternalAlignment(g124,g127)
    c: InternalAlignment(g125,g127)
    c: InternalAlignment(g126,g127)
    c: InternalAlignment(g128,g127)
    c: InternalAlignment(g129,g127)
    c: Block(g121)
    c: Block(g127)
    c: Coincident(g130,g121)
    c: Coincident(g130,g127)
    c: Vertical(g130)
    c: Coincident(g131,g127)
    c: Coincident(g131,g64)
    c: Coincident(g132,g64)
    c: Coincident(g132,g121)
    c: Weight(g133) = 1
    c: Equal(g133,g134)
    c: Equal(g133,g135)
    c: InternalAlignment(g133,g136)
    c: InternalAlignment(g134,g136)
    c: InternalAlignment(g135,g136)
    c: InternalAlignment(g137,g136)
    c: InternalAlignment(g138,g136)
    c: Weight(g139) = 1
    c: Equal(g139,g140)
    c: Equal(g139,g141)
    c: InternalAlignment(g139,g142)
    c: InternalAlignment(g140,g142)
    c: InternalAlignment(g141,g142)
    c: InternalAlignment(g143,g142)
    c: InternalAlignment(g144,g142)
    c: Weight(g145) = 1
    c: Equal(g145,g146)
    c: Equal(g145,g147)
    c: InternalAlignment(g145,g148)
    c: InternalAlignment(g146,g148)
    c: InternalAlignment(g147,g148)
    c: InternalAlignment(g149,g148)
    c: InternalAlignment(g150,g148)
    c: Weight(g151) = 1
    c: Equal(g151,g152)
    c: Equal(g151,g153)
    c: InternalAlignment(g151,g154)
    c: InternalAlignment(g152,g154)
    c: InternalAlignment(g153,g154)
    c: InternalAlignment(g155,g154)
    c: InternalAlignment(g156,g154)
    c: Block(g154)
    c: Block(g148)
    c: Block(g142)
    c: Block(g136)
    c: Coincident(g157,g31)
    c: Coincident(g157,g154)
    c: Coincident(g158,g154)
    c: Coincident(g158,g148)
    c: Horizontal(g158)
    c: Coincident(g159,g148)
    c: Coincident(g159,g31)
    c: Vertical(g159)
    c: Coincident(g160,g25)
    c: Coincident(g160,g142)
    c: Vertical(g160)
    c: Coincident(g161,g142)
    c: Coincident(g161,g136)
    c: Horizontal(g161)
    c: Coincident(g162,g136)
    c: Coincident(g162,g25)
    c: Weight(g163) = 1
    c: Equal(g163,g164)
    c: Equal(g163,g165)
    c: InternalAlignment(g163,g166)
    c: InternalAlignment(g164,g166)
    c: InternalAlignment(g165,g166)
    c: InternalAlignment(g167,g166)
    c: InternalAlignment(g168,g166)
    c: Weight(g169) = 1
    c: Equal(g169,g170)
    c: Equal(g169,g171)
    c: InternalAlignment(g169,g172)
    c: InternalAlignment(g170,g172)
    c: InternalAlignment(g171,g172)
    c: InternalAlignment(g173,g172)
    c: InternalAlignment(g174,g172)
    c: Weight(g175) = 1
    c: Equal(g175,g176)
    c: Equal(g175,g177)
    c: InternalAlignment(g175,g178)
    c: InternalAlignment(g176,g178)
    c: InternalAlignment(g177,g178)
    c: InternalAlignment(g179,g178)
    c: InternalAlignment(g180,g178)
    c: Weight(g181) = 1
    c: Equal(g181,g182)
    c: Equal(g181,g183)
    c: InternalAlignment(g181,g184)
    c: InternalAlignment(g182,g184)
    c: InternalAlignment(g183,g184)
    c: InternalAlignment(g185,g184)
    c: InternalAlignment(g186,g184)
    c: Block(g184)
    c: Block(g178)
    c: Block(g172)
    c: Block(g166)
    c: Coincident(g187,g184)
    c: Coincident(g187,g178)
    c: Horizontal(g187)
    c: Coincident(g188,g178)
    c: Coincident(g188,g13)
    c: Vertical(g188)
    c: Coincident(g189,g19)
    c: Coincident(g189,g172)
    c: Vertical(g189)
    c: Coincident(g190,g172)
    c: Coincident(g190,g166)
    c: Horizontal(g190)
    c: Coincident(g191,g166)
    c: Coincident(g191,g19)
    c: Coincident(g192,g13)
    c: Weight(g193) = 1
    c: Equal(g193,g194)
    c: Equal(g193,g195)
    c: InternalAlignment(g193,g196)
    c: InternalAlignment(g194,g196)
    c: InternalAlignment(g195,g196)
    c: InternalAlignment(g197,g196)
    c: InternalAlignment(g198,g196)
    c: Weight(g199) = 1
    c: Equal(g199,g200)
    c: Equal(g199,g201)
    c: InternalAlignment(g199,g202)
    c: InternalAlignment(g200,g202)
    c: InternalAlignment(g201,g202)
    c: InternalAlignment(g203,g202)
    c: InternalAlignment(g204,g202)
    c: Block(g202)
    c: Block(g196)
    c: Coincident(g205,g202)
    c: Coincident(g205,g37)
    c: Coincident(g206,g37)
    c: Coincident(g206,g196)
    c: Coincident(g207,g196)
    c: Coincident(g207,g202)
    c: Vertical(g207)
    c: Weight(g208) = 1
    c: Equal(g208,g209)
    c: Equal(g208,g210)
    c: InternalAlignment(g208,g211)
    c: InternalAlignment(g209,g211)
    c: InternalAlignment(g210,g211)
    c: InternalAlignment(g212,g211)
    c: InternalAlignment(g213,g211)
    c: Weight(g214) = 1
    c: Equal(g214,g215)
    c: Equal(g214,g216)
    c: InternalAlignment(g214,g217)
    c: InternalAlignment(g215,g217)
    c: InternalAlignment(g216,g217)
    c: InternalAlignment(g218,g217)
    c: InternalAlignment(g219,g217)
    c: Block(g217)
    c: Block(g211)
    c: Coincident(g220,g211)
    c: Coincident(g220,g43)
    c: Coincident(g221,g43)
    c: Coincident(g221,g217)
    c: Coincident(g222,g217)
    c: Coincident(g222,g211)
    c: Vertical(g222)
    c: Horizontal(g223)
    c: Block(g223)
    c: Vertical(g224)
    c: Block(g224)
    c: Block(g225)
    c: Weight(g226) = 1
    c: Equal(g226,g227)
    c: Equal(g226,g228)
    c: InternalAlignment(g226,g229)
    c: InternalAlignment(g227,g229)
    c: InternalAlignment(g228,g229)
    c: InternalAlignment(g230,g229)
    c: InternalAlignment(g231,g229)
    c: Weight(g232) = 1
    c: Equal(g232,g233)
    c: Equal(g232,g234)
    c: InternalAlignment(g232,g235)
    c: InternalAlignment(g233,g235)
    c: InternalAlignment(g234,g235)
    c: InternalAlignment(g236,g235)
    c: InternalAlignment(g237,g235)
    c: Weight(g238) = 1
    c: Equal(g238,g239)
    c: Equal(g238,g240)
    c: InternalAlignment(g238,g241)
    c: InternalAlignment(g239,g241)
    c: InternalAlignment(g240,g241)
    c: InternalAlignment(g242,g241)
    c: InternalAlignment(g243,g241)
    c: Weight(g244) = 1
    c: Equal(g244,g245)
    c: Equal(g244,g246)
    c: InternalAlignment(g244,g247)
    c: InternalAlignment(g245,g247)
    c: InternalAlignment(g246,g247)
    c: InternalAlignment(g248,g247)
    c: InternalAlignment(g249,g247)
    c: Block(g229)
    c: Block(g235)
    c: Block(g241)
    c: Block(g247)
    c: Coincident(g250,g235)
    c: Coincident(g250,g229)
    c: Horizontal(g250)
    c: Block(g192)
    c: Weight(g251) = 1
    c: Equal(g251,g252)
    c: Equal(g251,g253)
    c: InternalAlignment(g251,g254)
    c: InternalAlignment(g252,g254)
    c: InternalAlignment(g253,g254)
    c: InternalAlignment(g255,g254)
    c: InternalAlignment(g256,g254)
    c: Weight(g257) = 1
    c: Equal(g257,g258)
    c: Equal(g257,g259)
    c: InternalAlignment(g257,g260)
    c: InternalAlignment(g258,g260)
    c: InternalAlignment(g259,g260)
    c: InternalAlignment(g261,g260)
    c: InternalAlignment(g262,g260)
    c: Block(g254)
    c: Block(g260)
    c: Coincident(g263,g254)
    c: Coincident(g263,g260)
    c: Weight(g264) = 1
    c: Equal(g264,g265)
    c: Equal(g264,g266)
    c: InternalAlignment(g264,g267)
    c: InternalAlignment(g265,g267)
    c: InternalAlignment(g266,g267)
    c: InternalAlignment(g268,g267)
    c: InternalAlignment(g269,g267)
    c: Weight(g270) = 1
    c: Equal(g270,g271)
    c: Equal(g270,g272)
    c: InternalAlignment(g270,g273)
    c: InternalAlignment(g271,g273)
    c: InternalAlignment(g272,g273)
    c: InternalAlignment(g274,g273)
    c: InternalAlignment(g275,g273)
    c: Weight(g276) = 1
    c: Equal(g276,g277)
    c: Equal(g276,g278)
    c: InternalAlignment(g276,g279)
    c: InternalAlignment(g277,g279)
    c: InternalAlignment(g278,g279)
    c: InternalAlignment(g280,g279)
    c: InternalAlignment(g281,g279)
    c: Block(g279)
    c: Block(g273)
    c: Block(g267)
    c: Coincident(g282,g273)
    c: Coincident(g282,g267)
    c: Coincident(g283,g267)
    c: Coincident(g283,g279)
    c: Vertical(g283)
    c: Coincident(g284,g279)
    c: Coincident(g284,g273)
    c: Horizontal(g284)
    c: Weight(g285) = 1
    c: Equal(g285,g286)
    c: InternalAlignment(g285,g287)
    c: InternalAlignment(g286,g287)
    c: InternalAlignment(g288,g287)
    c: InternalAlignment(g289,g287)
    c: Weight(g290) = 1
    c: InternalAlignment(g291,g293)
    c: InternalAlignment(g292,g293)
    c: InternalAlignment(g294,g293)
    c: InternalAlignment(g295,g293)
    c: Weight(g296) = 1
    c: Equal(g296,g297)
    c: Equal(g296,g298)
    c: InternalAlignment(g296,g299)
    c: InternalAlignment(g297,g299)
    c: InternalAlignment(g298,g299)
    c: InternalAlignment(g300,g299)
    c: InternalAlignment(g301,g299)
    c: Equal(g302,g303)
    c: Equal(g302,g304)
    c: InternalAlignment(g302,g305)
    c: InternalAlignment(g303,g305)
    c: InternalAlignment(g304,g305)
    c: InternalAlignment(g306,g305)
    c: InternalAlignment(g307,g305)
    c: Block(g293)
    c: Block(g299)
    c: Block(g305)
    c: Block(g287)
    c: Coincident(g308,g287)
    c: Coincident(g308,g293)
    c: Horizontal(g308)
    c: Coincident(g309,g293)
    c: Coincident(g309,g299)
    c: Vertical(g309)
    c: Coincident(g310,g299)
    c: Coincident(g310,g305)
    c: Horizontal(g310)
    c: Coincident(g311,g305)
    c: Coincident(g311,g287)
    c: Weight(g312) = 1
    c: Equal(g312,g313)
    c: Equal(g312,g314)
    c: InternalAlignment(g312,g315)
    c: InternalAlignment(g313,g315)
    c: InternalAlignment(g314,g315)
    c: InternalAlignment(g316,g315)
    c: InternalAlignment(g317,g315)
    c: Weight(g318) = 1
    c: Equal(g318,g319)
    c: Equal(g318,g320)
    c: InternalAlignment(g318,g321)
    c: InternalAlignment(g319,g321)
    c: InternalAlignment(g320,g321)
    c: InternalAlignment(g322,g321)
    c: InternalAlignment(g323,g321)
    c: Weight(g324) = 1
    c: Equal(g324,g325)
    c: Equal(g324,g326)
    c: InternalAlignment(g324,g327)
    c: InternalAlignment(g325,g327)
    c: InternalAlignment(g326,g327)
    c: InternalAlignment(g328,g327)
    c: InternalAlignment(g329,g327)
    c: Block(g327)
    c: Block(g321)
    c: Block(g315)
    c: Coincident(g330,g327)
    c: Coincident(g330,g321)
    c: Horizontal(g330)
    c: Coincident(g331,g321)
    c: Coincident(g331,g315)
    c: Vertical(g331)
    c: Coincident(g332,g315)
    c: Coincident(g332,g327)
    c: InternalAlignment(g333,g334)
    c: InternalAlignment(g335,g334)
    c: InternalAlignment(g336,g334)
    c: Block(g334)
    c: Equal(g337,g338)
    c: Equal(g337,g339)
    c: InternalAlignment(g337,g340)
    c: InternalAlignment(g338,g340)
    c: InternalAlignment(g339,g340)
    c: InternalAlignment(g341,g340)
    c: InternalAlignment(g342,g340)
    c: Block(g340)
    c: Coincident(g343,g334)
    c: Horizontal(g343)
    c: Block(g343)
    c: Coincident(g344,g334)
    c: Coincident(g344,g260)
    c: Vertical(g344)
    c: Coincident(g345,g340)
    c: Coincident(g345,g254)
    c: Vertical(g345)
    c: Coincident(g347,g5)
    c: Coincident(g348,g5)
    c: Block(g346)
    c: Block(g5)
    c: Block(g348)
    c: Block(g347)
    c: Distance(g344) = 119.89
FEATURE [Sketcher::SketchObject] Sketch001
  FullyConstrained = true
  MapMode = 4
  Placement = pos=(0,0,0) rot=(0.57735,0.57735,0.57735;2.0944rad)
  Support = -> [Sketch]
  sketch-geometry (46):
    g0: BSplineCurve PolesCount=3 KnotsCount=2 Degree=2 IsPeriodic=0
    g1: ArcOfCircle CenterX=73.1223 CenterY=-32.291 CenterZ=0 NormalX=0 NormalY=0 NormalZ=1 AngleXU=0 Radius=13 StartAngle=5.92268 EndAngle=9.06428
    g2: ArcOfCircle CenterX=66.7816 CenterY=-49.1439 CenterZ=0 NormalX=0 NormalY=0 NormalZ=1 AngleXU=0 Radius=13 StartAngle=2.78068 EndAngle=5.92131
    g3: ArcOfCircle CenterX=55.9263 CenterY=-78.1807 CenterZ=0 NormalX=0 NormalY=0 NormalZ=1 AngleXU=0 Radius=13 StartAngle=5.92268 EndAngle=9.06428
    g4: ArcOfCircle CenterX=49.5884 CenterY=-95.0342 CenterZ=0 NormalX=0 NormalY=0 NormalZ=1 AngleXU=0 Radius=13 StartAngle=2.78068 EndAngle=5.92131
    g5: ArcOfCircle CenterX=38.7206 CenterY=-124.067 CenterZ=0 NormalX=0 NormalY=0 NormalZ=1 AngleXU=0 Radius=13 StartAngle=5.92268 EndAngle=9.06428
    g6: ArcOfCircle CenterX=32.3875 CenterY=-140.92 CenterZ=0 NormalX=0 NormalY=0 NormalZ=1 AngleXU=0 Radius=13 StartAngle=2.78068 EndAngle=5.92131
    g7: ArcOfCircle CenterX=21.4715 CenterY=-169.934 CenterZ=0 NormalX=0 NormalY=0 NormalZ=1 AngleXU=0 Radius=13 StartAngle=5.92268 EndAngle=9.06428
    g8: ArcOfCircle CenterX=15.1336 CenterY=-186.787 CenterZ=0 NormalX=0 NormalY=0 NormalZ=1 AngleXU=0 Radius=13 StartAngle=2.78068 EndAngle=5.92131
    g9-g12: Circle x4 (B-spline internal-alignment scaffolding for g13; pole/knot coordinates omitted)
    g13: BSplineCurve PolesCount=4 KnotsCount=2 Degree=3 IsPeriodic=0
    g14: GeomPoint X=28.8094 Y=-19.0875 Z=0
    g15: GeomPoint X=47.0443 Y=-50.4712 Z=0
    g16: Circle CenterX=53.5586 CenterY=-23.2695 CenterZ=0 NormalX=0 NormalY=0 NormalZ=1 AngleXU=0 Radius=3.24518
    g17: Circle CenterX=-195.441 CenterY=-127.082 CenterZ=0 NormalX=0 NormalY=0 NormalZ=1 AngleXU=0 Radius=1
    g18: Circle CenterX=-8.24091 CenterY=-197.481 CenterZ=0 NormalX=0 NormalY=0 NormalZ=1 AngleXU=0 Radius=1
    g19: Circle CenterX=12.8789 CenterY=-141.321 CenterZ=0 NormalX=0 NormalY=0 NormalZ=1 AngleXU=0 Radius=1
    g20: BSplineCurve PolesCount=3 KnotsCount=2 Degree=2 IsPeriodic=0
    g21: GeomPoint X=-195.441 Y=-127.082 Z=0
    g22: GeomPoint X=12.8789 Y=-141.321 Z=0
    g23: Circle CenterX=-12.8016 CenterY=-179.036 CenterZ=0 NormalX=0 NormalY=0 NormalZ=1 AngleXU=0 Radius=10.5072
    g24: Circle CenterX=0.933922 CenterY=-166.43 CenterZ=0 NormalX=0 NormalY=0 NormalZ=1 AngleXU=0 Radius=3.26661
    g25: Circle CenterX=-33.5518 CenterY=-176.44 CenterZ=0 NormalX=0 NormalY=0 NormalZ=1 AngleXU=0 Radius=5.64388
    g26: Circle CenterX=-47.2366 CenterY=-173.859 CenterZ=0 NormalX=0 NormalY=0 NormalZ=1 AngleXU=0 Radius=3.01653
    g27: Circle CenterX=-56.2595 CenterY=-171.456 CenterZ=0 NormalX=0 NormalY=0 NormalZ=1 AngleXU=0 Radius=2.12826
    g28: ArcOfCircle CenterX=51.2151 CenterY=-198.473 CenterZ=0 NormalX=0 NormalY=0 NormalZ=1 AngleXU=0 Radius=20 StartAngle=2.78189 EndAngle=4.35269
    g29: LineSegment StartX=32.4951 StartY=-191.433 StartZ=0 EndX=94.6578 EndY=-26.1352 EndZ=0
    g30: LineSegment StartX=43.1192 StartY=-220.001 StartZ=0 EndX=-196.497 EndY=-129.89 EndZ=0
    g31: LineSegment StartX=43.1192 StartY=-220.001 StartZ=0 EndX=44.1752 EndY=-217.193 EndZ=0
    g32: LineSegment StartX=117.223 StartY=-19.0875 StartZ=0 EndX=117.223 EndY=-16.0875 EndZ=0
    g33: LineSegment StartX=117.223 StartY=-16.0875 StartZ=0 EndX=17.2232 EndY=-16.0875 EndZ=0
    g34: LineSegment StartX=17.2232 StartY=-16.0875 StartZ=0 EndX=17.2232 EndY=-19.0875 EndZ=0
    g35: LineSegment StartX=28.8094 StartY=-19.0875 StartZ=0 EndX=17.2232 EndY=-19.0875 EndZ=0
    g36: LineSegment StartX=47.0443 StartY=-50.4712 StartZ=0 EndX=12.8789 EndY=-141.321 EndZ=0
    g37: LineSegment StartX=-195.441 StartY=-127.082 StartZ=0 EndX=-196.497 EndY=-129.89 EndZ=0
    g38: LineSegment StartX=85.2866 StartY=-36.8766 StartZ=0 EndX=78.9396 EndY=-53.7463 EndZ=0
    g39: LineSegment StartX=60.9579 StartY=-27.7053 StartZ=0 EndX=54.6191 EndY=-44.5532 EndZ=0
    g40: LineSegment StartX=68.0907 StartY=-82.7664 StartZ=0 EndX=61.7465 EndY=-99.6365 EndZ=0
    g41: LineSegment StartX=43.7619 StartY=-73.595 StartZ=0 EndX=37.426 EndY=-90.4435 EndZ=0
    g42: LineSegment StartX=50.885 StartY=-128.652 StartZ=0 EndX=44.5456 EndY=-145.522 EndZ=0
    g43: LineSegment StartX=26.5562 StartY=-119.481 StartZ=0 EndX=20.2251 EndY=-136.329 EndZ=0
    g44: LineSegment StartX=9.3071 StartY=-165.349 StartZ=0 EndX=2.97115 EndY=-182.197 EndZ=0
    g45: LineSegment StartX=33.6358 StartY=-174.52 StartZ=0 EndX=27.2917 EndY=-191.39 EndZ=0
  constraints (71):
    c: Block(g0)
    c: Block(g1)
    c: Block(g2)
    c: Block(g4)
    c: Block(g3)
    c: Block(g6)
    c: Block(g5)
    c: Block(g8)
    c: Block(g7)
    c: Weight(g9) = 1
    c: Equal(g9,g10)
    c: Equal(g9,g11)
    c: Equal(g9,g12)
    c: InternalAlignment(g9-g12 -> g13) x4
    c: InternalAlignment(g14,g13)
    c: InternalAlignment(g15,g13)
    c: Block(g16)
    c: Weight(g17) = 1
    c: Equal(g17,g18)
    c: Equal(g17,g19)
    c: InternalAlignment(g17,g20)
    c: InternalAlignment(g18,g20)
    c: InternalAlignment(g19,g20)
    c: InternalAlignment(g21,g20)
    c: InternalAlignment(g22,g20)
    c: Block(g20)
    c: Block(g23)
    c: Block(g24)
    c: Block(g25)
    c: Block(g26)
    c: Block(g27)
    c: Block(g28)
    c: Coincident(g29,g28)
    c: Coincident(g29,g0)
    c: Block(g13)
    c: Coincident(g31,g30)
    c: Coincident(g31,g28)
    c: Block(g31)
    c: Coincident(g32,g0)
    c: Vertical(g32)
    c: Coincident(g33,g32)
    c: Horizontal(g33)
    c: Coincident(g34,g33)
    c: Vertical(g34)
    c: Block(g33)
    c: Coincident(g35,g13)
    c: Coincident(g35,g34)
    c: Horizontal(g35)
    c: Coincident(g36,g13)
    c: Coincident(g36,g20)
    c: Coincident(g37,g20)
    c: Coincident(g37,g30)
    c: Block(g30)
    c: Coincident(g38,g1)
    c: Coincident(g38,g2)
    c: Coincident(g39,g1)
    c: Coincident(g39,g2)
    c: Coincident(g40,g3)
    c: Coincident(g40,g4)
    c: Coincident(g41,g3)
    c: Coincident(g41,g4)
    c: Coincident(g42,g5)
    c: Coincident(g42,g6)
    c: Coincident(g43,g5)
    c: Coincident(g43,g6)
    c: Coincident(g44,g7)
    c: Coincident(g44,g8)
    c: Coincident(g45,g7)
    c: Coincident(g45,g8)
    c: Distance(g30) = 256
    c: Distance(g33) = 100
FEATURE [Part::Extrusion] Extrude002
  Base = -> Sketch001
  Dir = (1,0,0)
  DirMode = 2
  FaceMakerClass = Part::FaceMakerBullseye
  LengthFwd = 8
  LengthRev = 0
  Solid = true
  Symmetric = false
FEATURE [Sketcher::SketchObject] Sketch002
  FullyConstrained = true
  sketch-geometry (20):
    g0: LineSegment StartX=-2.77179 StartY=-200.304 StartZ=0 EndX=5.22821 EndY=-200.304 EndZ=0
    g1: LineSegment StartX=5.22821 StartY=-200.304 StartZ=0 EndX=5.22821 EndY=-197.304 EndZ=0
    g2: LineSegment StartX=-2.77179 StartY=-200.304 StartZ=0 EndX=-2.77179 EndY=-197.304 EndZ=0
    g3: LineSegment StartX=5.22821 StartY=-197.304 StartZ=0 EndX=8.22821 EndY=-197.304 EndZ=0
    g4: LineSegment StartX=-2.77179 StartY=-197.304 StartZ=0 EndX=-5.77179 EndY=-197.304 EndZ=0
    g5: LineSegment StartX=19.2282 StartY=-203.304 StartZ=0 EndX=19.2282 EndY=-206.304 EndZ=0
    g6: LineSegment StartX=-16.7718 StartY=-203.304 StartZ=0 EndX=-16.7718 EndY=-206.304 EndZ=0
    g7: LineSegment StartX=-16.7718 StartY=-206.304 StartZ=0 EndX=19.2282 EndY=-206.304 EndZ=0
    g8: Circle CenterX=-16.7718 CenterY=-203.304 CenterZ=0 NormalX=0 NormalY=0 NormalZ=1 AngleXU=0 Radius=1
    g9: Circle CenterX=-5.77179 CenterY=-203.304 CenterZ=0 NormalX=0 NormalY=0 NormalZ=1 AngleXU=0 Radius=1
    g10: Circle CenterX=-5.77179 CenterY=-197.304 CenterZ=0 NormalX=0 NormalY=0 NormalZ=1 AngleXU=0 Radius=1
    g11: BSplineCurve PolesCount=3 KnotsCount=2 Degree=2 IsPeriodic=0
    g12: GeomPoint X=-16.7718 Y=-203.304 Z=0
    g13: GeomPoint X=-5.77179 Y=-197.304 Z=0
    g14: Circle CenterX=19.2282 CenterY=-203.304 CenterZ=0 NormalX=0 NormalY=0 NormalZ=1 AngleXU=0 Radius=1
    g15: Circle CenterX=8.22821 CenterY=-203.304 CenterZ=0 NormalX=0 NormalY=0 NormalZ=1 AngleXU=0 Radius=1
    g16: Circle CenterX=8.22821 CenterY=-197.304 CenterZ=0 NormalX=0 NormalY=0 NormalZ=1 AngleXU=0 Radius=1
    g17: BSplineCurve PolesCount=3 KnotsCount=2 Degree=2 IsPeriodic=0
    g18: GeomPoint X=19.2282 Y=-203.304 Z=0
    g19: GeomPoint X=8.22821 Y=-197.304 Z=0
  constraints (41):
    c: Horizontal(g0)
    c: Distance(g0) = 8
    c: Coincident(g1,g0)
    c: Vertical(g1)
    c: Distance(g1) = 3
    c: Coincident(g2,g0)
    c: Vertical(g2)
    c: Distance(g2) = 3
    c: Coincident(g3,g1)
    c: Horizontal(g3)
    c: Distance(g3) = 3
    c: Coincident(g4,g2)
    c: Horizontal(g4)
    c: Distance(g4) = 3
    c: Vertical(g5)
    c: Vertical(g6)
    c: Coincident(g7,g6)
    c: Coincident(g7,g5)
    c: Weight(g8) = 1
    c: Equal(g8,g9)
    c: Equal(g8,g10)
    c: Coincident(g11,g4)
    c: InternalAlignment(g8,g11)
    c: InternalAlignment(g9,g11)
    c: InternalAlignment(g10,g11)
    c: InternalAlignment(g12,g11)
    c: InternalAlignment(g13,g11)
    c: Coincident(g17,g5)
    c: Weight(g14) = 1
    c: Equal(g14,g15)
    c: Equal(g14,g16)
    c: Coincident(g17,g3)
    c: InternalAlignment(g14,g17)
    c: InternalAlignment(g15,g17)
    c: InternalAlignment(g16,g17)
    c: InternalAlignment(g18,g17)
    c: InternalAlignment(g19,g17)
    c: Block(g7)
    c: Block(g17)
    c: Block(g11)
    c: Block(g6)
FEATURE [Part::Extrusion] Extrude003
  Base = -> Sketch002
  Dir = (0,0,1)
  DirMode = 2
  FaceMakerClass = Part::FaceMakerBullseye
  LengthFwd = 260
  LengthRev = 0
  Solid = true
  Symmetric = false
FEATURE [Sketcher::SketchObject] Sketch003
  FullyConstrained = false
  sketch-geometry (395):
    g0: LineSegment StartX=-42.9272 StartY=136.221 StartZ=0 EndX=-42.9272 EndY=-103.779 EndZ=0
    g1: LineSegment StartX=407.073 StartY=136.221 StartZ=0 EndX=407.073 EndY=-103.779 EndZ=0
    g2: ArcOfCircle CenterX=-26.9272 CenterY=-83.7794 CenterZ=0 NormalX=0 NormalY=0 NormalZ=1 AngleXU=0 Radius=8 StartAngle=3.14159 EndAngle=6.28319
    g3: ArcOfCircle CenterX=391.073 CenterY=-83.7794 CenterZ=0 NormalX=0 NormalY=0 NormalZ=1 AngleXU=0 Radius=8 StartAngle=3.14159 EndAngle=6.28319
    g4: Circle CenterX=175.022 CenterY=27.0628 CenterZ=0 NormalX=0 NormalY=0 NormalZ=1 AngleXU=0 Radius=1
    g5: Circle CenterX=179.022 CenterY=24.8665 CenterZ=0 NormalX=0 NormalY=0 NormalZ=1 AngleXU=0 Radius=1
    g6: Circle CenterX=179.022 CenterY=27.0628 CenterZ=0 NormalX=0 NormalY=0 NormalZ=1 AngleXU=0 Radius=1
    g7: BSplineCurve PolesCount=3 KnotsCount=2 Degree=2 IsPeriodic=0
    g8: GeomPoint X=175.022 Y=27.0628 Z=0
    g9: GeomPoint X=179.022 Y=27.0628 Z=0
    g10: Circle CenterX=189.124 CenterY=27.0628 CenterZ=0 NormalX=0 NormalY=0 NormalZ=1 AngleXU=0 Radius=1
    g11: Circle CenterX=185.124 CenterY=24.8665 CenterZ=0 NormalX=0 NormalY=0 NormalZ=1 AngleXU=0 Radius=1
    g12: Circle CenterX=185.124 CenterY=27.0628 CenterZ=0 NormalX=0 NormalY=0 NormalZ=1 AngleXU=0 Radius=1
    g13: BSplineCurve PolesCount=3 KnotsCount=2 Degree=2 IsPeriodic=0
    g14: GeomPoint X=189.124 Y=27.0628 Z=0
    g15: GeomPoint X=185.124 Y=27.0628 Z=0
    g16: Circle CenterX=175.022 CenterY=5.37834 CenterZ=0 NormalX=0 NormalY=0 NormalZ=1 AngleXU=0 Radius=1
    g17: Circle CenterX=179.022 CenterY=7.57463 CenterZ=0 NormalX=0 NormalY=0 NormalZ=1 AngleXU=0 Radius=1
    g18: Circle CenterX=179.022 CenterY=5.34704 CenterZ=0 NormalX=0 NormalY=0 NormalZ=1 AngleXU=0 Radius=1
    g19: BSplineCurve PolesCount=3 KnotsCount=2 Degree=2 IsPeriodic=0
    g20: GeomPoint X=175.022 Y=5.37834 Z=0
    g21: GeomPoint X=179.022 Y=5.34704 Z=0
    g22: Circle CenterX=189.124 CenterY=5.37834 CenterZ=0 NormalX=0 NormalY=0 NormalZ=1 AngleXU=0 Radius=1
    g23: Circle CenterX=185.124 CenterY=7.57463 CenterZ=0 NormalX=0 NormalY=0 NormalZ=1 AngleXU=0 Radius=1
    g24: Circle CenterX=185.124 CenterY=5.34704 CenterZ=0 NormalX=0 NormalY=0 NormalZ=1 AngleXU=0 Radius=1
    g25: BSplineCurve PolesCount=3 KnotsCount=2 Degree=2 IsPeriodic=0
    g26: GeomPoint X=189.124 Y=5.37834 Z=0
    g27: GeomPoint X=185.124 Y=5.34704 Z=0
    g28: Circle CenterX=165.871 CenterY=18.1458 CenterZ=0 NormalX=0 NormalY=0 NormalZ=1 AngleXU=0 Radius=1
    g29: Circle CenterX=169.377 CenterY=16.2206 CenterZ=0 NormalX=0 NormalY=0 NormalZ=1 AngleXU=0 Radius=1
    g30: Circle CenterX=165.871 CenterY=14.2954 CenterZ=0 NormalX=0 NormalY=0 NormalZ=1 AngleXU=0 Radius=1
    g31: BSplineCurve PolesCount=3 KnotsCount=2 Degree=2 IsPeriodic=0
    g32: GeomPoint X=165.871 Y=18.1458 Z=0
    g33: GeomPoint X=165.871 Y=14.2954 Z=0
    g34: Circle CenterX=198.275 CenterY=18.1458 CenterZ=0 NormalX=0 NormalY=0 NormalZ=1 AngleXU=0 Radius=1
    g35: Circle CenterX=194.768 CenterY=16.2206 CenterZ=0 NormalX=0 NormalY=0 NormalZ=1 AngleXU=0 Radius=1
    g36: Circle CenterX=198.275 CenterY=14.2954 CenterZ=0 NormalX=0 NormalY=0 NormalZ=1 AngleXU=0 Radius=1
    g37: BSplineCurve PolesCount=3 KnotsCount=2 Degree=2 IsPeriodic=0
    g38: GeomPoint X=198.275 Y=18.1458 Z=0
    g39: GeomPoint X=198.275 Y=14.2954 Z=0
    g40: LineSegment StartX=407.073 StartY=-103.779 StartZ=0 EndX=-42.9272 EndY=-103.779 EndZ=0
    g41: Circle CenterX=125.607 CenterY=54.1951 CenterZ=0 NormalX=0 NormalY=0 NormalZ=1 AngleXU=0 Radius=1
    g42: Circle CenterX=139.632 CenterY=46.4944 CenterZ=0 NormalX=0 NormalY=0 NormalZ=1 AngleXU=0 Radius=1
    g43: Circle CenterX=127.326 CenterY=56.7187 CenterZ=0 NormalX=0 NormalY=0 NormalZ=1 AngleXU=0 Radius=1
    g44: BSplineCurve PolesCount=3 KnotsCount=2 Degree=2 IsPeriodic=0
    g45: GeomPoint X=125.607 Y=54.1951 Z=0
    g46: GeomPoint X=127.326 Y=56.7187 Z=0
    g47: Circle CenterX=236.821 CenterY=56.7187 CenterZ=0 NormalX=0 NormalY=0 NormalZ=1 AngleXU=0 Radius=1
    g48: Circle CenterX=224.513 CenterY=46.4944 CenterZ=0 NormalX=0 NormalY=0 NormalZ=1 AngleXU=0 Radius=1
    g49: Circle CenterX=238.538 CenterY=54.1951 CenterZ=0 NormalX=0 NormalY=0 NormalZ=1 AngleXU=0 Radius=1
    g50: BSplineCurve PolesCount=3 KnotsCount=2 Degree=2 IsPeriodic=0
    g51: GeomPoint X=236.821 Y=56.7187 Z=0
    g52: GeomPoint X=238.538 Y=54.1951 Z=0
    g53: Circle CenterX=238.538 CenterY=-21.7539 CenterZ=0 NormalX=0 NormalY=0 NormalZ=1 AngleXU=0 Radius=1
    g54: Circle CenterX=224.513 CenterY=-14.0532 CenterZ=0 NormalX=0 NormalY=0 NormalZ=1 AngleXU=0 Radius=1
    g55: Circle CenterX=236.821 CenterY=-24.2775 CenterZ=0 NormalX=0 NormalY=0 NormalZ=1 AngleXU=0 Radius=1
    g56: BSplineCurve PolesCount=3 KnotsCount=2 Degree=2 IsPeriodic=0
    g57: GeomPoint X=238.538 Y=-21.7539 Z=0
    g58: GeomPoint X=236.821 Y=-24.2775 Z=0
    g59: Circle CenterX=125.607 CenterY=-21.7539 CenterZ=0 NormalX=0 NormalY=0 NormalZ=1 AngleXU=0 Radius=1
    g60: Circle CenterX=139.632 CenterY=-14.0532 CenterZ=0 NormalX=0 NormalY=0 NormalZ=1 AngleXU=0 Radius=1
    g61: Circle CenterX=127.325 CenterY=-24.2775 CenterZ=0 NormalX=0 NormalY=0 NormalZ=1 AngleXU=0 Radius=1
    g62: BSplineCurve PolesCount=3 KnotsCount=2 Degree=2 IsPeriodic=0
    g63: GeomPoint X=125.607 Y=-21.7539 Z=0
    g64: GeomPoint X=127.325 Y=-24.2775 Z=0
    g65: Circle CenterX=302.996 CenterY=111.695 CenterZ=0 NormalX=0 NormalY=0 NormalZ=1 AngleXU=0 Radius=1
    g66: Circle CenterX=306.073 CenterY=114.251 CenterZ=0 NormalX=0 NormalY=0 NormalZ=1 AngleXU=0 Radius=1
    g67: Circle CenterX=306.073 CenterY=110.251 CenterZ=0 NormalX=0 NormalY=0 NormalZ=1 AngleXU=0 Radius=1
    g68: BSplineCurve PolesCount=3 KnotsCount=2 Degree=2 IsPeriodic=0
    g69: GeomPoint X=302.996 Y=111.695 Z=0
    g70: GeomPoint X=306.073 Y=110.251 Z=0
    g71: Circle CenterX=306.073 CenterY=95.2763 CenterZ=0 NormalX=0 NormalY=0 NormalZ=1 AngleXU=0 Radius=1
    g72: Circle CenterX=306.073 CenterY=91.2763 CenterZ=0 NormalX=0 NormalY=0 NormalZ=1 AngleXU=0 Radius=1
    g73: Circle CenterX=302.567 CenterY=89.3511 CenterZ=0 NormalX=0 NormalY=0 NormalZ=1 AngleXU=0 Radius=1
    g74: BSplineCurve PolesCount=3 KnotsCount=2 Degree=2 IsPeriodic=0
    g75: GeomPoint X=306.073 Y=95.2763 Z=0
    g76: GeomPoint X=302.567 Y=89.3511 Z=0
    g77: LineSegment StartX=306.073 StartY=110.251 StartZ=0 EndX=306.073 EndY=95.2763 EndZ=0
    g78: LineSegment StartX=302.996 StartY=111.695 StartZ=0 EndX=236.821 EndY=56.7187 EndZ=0
    g79: LineSegment StartX=238.538 StartY=54.1951 StartZ=0 EndX=302.567 EndY=89.3511 EndZ=0
    g80: Circle CenterX=61.1496 CenterY=111.695 CenterZ=0 NormalX=0 NormalY=0 NormalZ=1 AngleXU=0 Radius=1
    g81: Circle CenterX=58.0728 CenterY=114.251 CenterZ=0 NormalX=0 NormalY=0 NormalZ=1 AngleXU=0 Radius=1
    g82: Circle CenterX=58.0728 CenterY=110.251 CenterZ=0 NormalX=0 NormalY=0 NormalZ=1 AngleXU=0 Radius=1
    g83: BSplineCurve PolesCount=3 KnotsCount=2 Degree=2 IsPeriodic=0
    g84: GeomPoint X=61.1496 Y=111.695 Z=0
    g85: GeomPoint X=58.0728 Y=110.251 Z=0
    g86: Circle CenterX=61.5791 CenterY=89.3511 CenterZ=0 NormalX=0 NormalY=0 NormalZ=1 AngleXU=0 Radius=1
    g87: Circle CenterX=58.0728 CenterY=91.2763 CenterZ=0 NormalX=0 NormalY=0 NormalZ=1 AngleXU=0 Radius=1
    g88: Circle CenterX=58.0728 CenterY=95.2763 CenterZ=0 NormalX=0 NormalY=0 NormalZ=1 AngleXU=0 Radius=1
    g89: BSplineCurve PolesCount=3 KnotsCount=2 Degree=2 IsPeriodic=0
    g90: GeomPoint X=61.5791 Y=89.3511 Z=0
    g91: GeomPoint X=58.0728 Y=95.2763 Z=0
    g92: LineSegment StartX=58.0728 StartY=110.251 StartZ=0 EndX=58.0728 EndY=95.2763 EndZ=0
    g93: LineSegment StartX=61.1496 StartY=111.695 StartZ=0 EndX=127.326 EndY=56.7187 EndZ=0
    g94: LineSegment StartX=125.607 StartY=54.1951 StartZ=0 EndX=61.5791 EndY=89.3511 EndZ=0
    g95: Circle CenterX=61.5791 CenterY=-56.9099 CenterZ=0 NormalX=0 NormalY=0 NormalZ=1 AngleXU=0 Radius=1
    g96: Circle CenterX=58.0728 CenterY=-58.8351 CenterZ=0 NormalX=0 NormalY=0 NormalZ=1 AngleXU=0 Radius=1
    g97: Circle CenterX=58.0728 CenterY=-62.8351 CenterZ=0 NormalX=0 NormalY=0 NormalZ=1 AngleXU=0 Radius=1
    g98: BSplineCurve PolesCount=3 KnotsCount=2 Degree=2 IsPeriodic=0
    g99: GeomPoint X=61.5791 Y=-56.9099 Z=0
    g100: GeomPoint X=58.0728 Y=-62.8351 Z=0
    g101: Circle CenterX=58.0728 CenterY=-77.8102 CenterZ=0 NormalX=0 NormalY=0 NormalZ=1 AngleXU=0 Radius=1
    g102: Circle CenterX=58.0728 CenterY=-81.8102 CenterZ=0 NormalX=0 NormalY=0 NormalZ=1 AngleXU=0 Radius=1
    g103: Circle CenterX=61.1496 CenterY=-79.2541 CenterZ=0 NormalX=0 NormalY=0 NormalZ=1 AngleXU=0 Radius=1
    g104: BSplineCurve PolesCount=3 KnotsCount=2 Degree=2 IsPeriodic=0
    g105: GeomPoint X=58.0728 Y=-77.8102 Z=0
    g106: GeomPoint X=61.1496 Y=-79.2541 Z=0
    g107: LineSegment StartX=58.0728 StartY=-62.8351 StartZ=0 EndX=58.0728 EndY=-77.8102 EndZ=0
    g108: LineSegment StartX=61.1496 StartY=-79.2541 StartZ=0 EndX=127.325 EndY=-24.2775 EndZ=0
    g109: LineSegment StartX=125.607 StartY=-21.7539 StartZ=0 EndX=61.5791 EndY=-56.9099 EndZ=0
    g110: Circle CenterX=302.567 CenterY=-56.9099 CenterZ=0 NormalX=0 NormalY=0 NormalZ=1 AngleXU=0 Radius=1
    g111: Circle CenterX=306.073 CenterY=-58.8351 CenterZ=0 NormalX=0 NormalY=0 NormalZ=1 AngleXU=0 Radius=1
    g112: Circle CenterX=306.073 CenterY=-62.8351 CenterZ=0 NormalX=0 NormalY=0 NormalZ=1 AngleXU=0 Radius=1
    g113: BSplineCurve PolesCount=3 KnotsCount=2 Degree=2 IsPeriodic=0
    g114: GeomPoint X=302.567 Y=-56.9099 Z=0
    g115: GeomPoint X=306.073 Y=-62.8351 Z=0
    g116: Circle CenterX=302.996 CenterY=-79.2541 CenterZ=0 NormalX=0 NormalY=0 NormalZ=1 AngleXU=0 Radius=1
    g117: Circle CenterX=306.073 CenterY=-81.8102 CenterZ=0 NormalX=0 NormalY=0 NormalZ=1 AngleXU=0 Radius=1
    g118: Circle CenterX=306.073 CenterY=-77.8102 CenterZ=0 NormalX=0 NormalY=0 NormalZ=1 AngleXU=0 Radius=1
    g119: BSplineCurve PolesCount=3 KnotsCount=2 Degree=2 IsPeriodic=0
    g120: GeomPoint X=302.996 Y=-79.2541 Z=0
    g121: GeomPoint X=306.073 Y=-77.8102 Z=0
    g122: LineSegment StartX=306.073 StartY=-62.8351 StartZ=0 EndX=306.073 EndY=-77.8102 EndZ=0
    g123: LineSegment StartX=302.996 StartY=-79.2541 StartZ=0 EndX=236.821 EndY=-24.2775 EndZ=0
    g124: LineSegment StartX=238.538 StartY=-21.7539 StartZ=0 EndX=302.567 EndY=-56.9099 EndZ=0
    g125: Circle CenterX=61.6457 CenterY=-88.8112 CenterZ=0 NormalX=0 NormalY=0 NormalZ=1 AngleXU=0 Radius=1
    g126: Circle CenterX=58.0728 CenterY=-91.7794 CenterZ=0 NormalX=0 NormalY=0 NormalZ=1 AngleXU=0 Radius=1
    g127: Circle CenterX=63.9135 CenterY=-91.7794 CenterZ=0 NormalX=0 NormalY=0 NormalZ=1 AngleXU=0 Radius=1
    g128: BSplineCurve PolesCount=3 KnotsCount=2 Degree=2 IsPeriodic=0
    g129: GeomPoint X=61.6457 Y=-88.8112 Z=0
    g130: GeomPoint X=63.9135 Y=-91.7794 Z=0
    g131: Circle CenterX=179.022 CenterY=-85.8163 CenterZ=0 NormalX=0 NormalY=0 NormalZ=1 AngleXU=0 Radius=1
    g132: Circle CenterX=179.022 CenterY=-91.7794 CenterZ=0 NormalX=0 NormalY=0 NormalZ=1 AngleXU=0 Radius=1
    g133: Circle CenterX=171.895 CenterY=-91.7794 CenterZ=0 NormalX=0 NormalY=0 NormalZ=1 AngleXU=0 Radius=1
    g134: BSplineCurve PolesCount=3 KnotsCount=2 Degree=2 IsPeriodic=0
    g135: GeomPoint X=179.022 Y=-85.8163 Z=0
    g136: GeomPoint X=171.895 Y=-91.7794 Z=0
    g137: Circle CenterX=185.124 CenterY=-86.2028 CenterZ=0 NormalX=0 NormalY=0 NormalZ=1 AngleXU=0 Radius=1
    g138: Circle CenterX=185.124 CenterY=-91.7794 CenterZ=0 NormalX=0 NormalY=0 NormalZ=1 AngleXU=0 Radius=1
    g139: Circle CenterX=191.747 CenterY=-91.7794 CenterZ=0 NormalX=0 NormalY=0 NormalZ=1 AngleXU=0 Radius=1
    g140: BSplineCurve PolesCount=3 KnotsCount=2 Degree=2 IsPeriodic=0
    g141: GeomPoint X=185.124 Y=-86.2028 Z=0
    g142: GeomPoint X=191.747 Y=-91.7794 Z=0
    g143: Circle CenterX=299.888 CenterY=-86.6413 CenterZ=0 NormalX=0 NormalY=0 NormalZ=1 AngleXU=0 Radius=1
    g144: Circle CenterX=306.073 CenterY=-91.7794 CenterZ=0 NormalX=0 NormalY=0 NormalZ=1 AngleXU=0 Radius=1
    g145: Circle CenterX=298.776 CenterY=-91.7794 CenterZ=0 NormalX=0 NormalY=0 NormalZ=1 AngleXU=0 Radius=1
    g146: BSplineCurve PolesCount=3 KnotsCount=2 Degree=2 IsPeriodic=0
    g147: GeomPoint X=299.888 Y=-86.6413 Z=0
    g148: GeomPoint X=298.776 Y=-91.7794 Z=0
    g149: LineSegment StartX=189.124 StartY=5.37834 StartZ=0 EndX=299.888 EndY=-86.6413 EndZ=0
    g150: LineSegment StartX=298.776 StartY=-91.7794 StartZ=0 EndX=191.747 EndY=-91.7794 EndZ=0
    g151: LineSegment StartX=185.124 StartY=-86.2028 StartZ=0 EndX=185.124 EndY=5.34704 EndZ=0
    g152: LineSegment StartX=179.022 StartY=5.34704 StartZ=0 EndX=179.022 EndY=-85.8163 EndZ=0
    g153: LineSegment StartX=171.895 StartY=-91.7794 StartZ=0 EndX=63.9135 EndY=-91.7794 EndZ=0
    g154: LineSegment StartX=61.6457 StartY=-88.8112 StartZ=0 EndX=175.022 EndY=5.37834 EndZ=0
    g155: Circle CenterX=302.073 CenterY=124.221 CenterZ=0 NormalX=0 NormalY=0 NormalZ=1 AngleXU=0 Radius=1
    g156: Circle CenterX=306.073 CenterY=124.221 CenterZ=0 NormalX=0 NormalY=0 NormalZ=1 AngleXU=0 Radius=1
    g157: Circle CenterX=302.996 CenterY=121.665 CenterZ=0 NormalX=0 NormalY=0 NormalZ=1 AngleXU=0 Radius=1
    g158: BSplineCurve PolesCount=3 KnotsCount=2 Degree=2 IsPeriodic=0
    g159: GeomPoint X=302.073 Y=124.221 Z=0
    g160: GeomPoint X=302.996 Y=121.665 Z=0
    g161: Circle CenterX=189.124 CenterY=124.221 CenterZ=0 NormalX=0 NormalY=0 NormalZ=1 AngleXU=0 Radius=1
    g162: Circle CenterX=185.124 CenterY=124.221 CenterZ=0 NormalX=0 NormalY=0 NormalZ=1 AngleXU=0 Radius=1
    g163: Circle CenterX=185.124 CenterY=120.221 CenterZ=0 NormalX=0 NormalY=0 NormalZ=1 AngleXU=0 Radius=1
    g164: BSplineCurve PolesCount=3 KnotsCount=2 Degree=2 IsPeriodic=0
    g165: GeomPoint X=189.124 Y=124.221 Z=0
    g166: GeomPoint X=185.124 Y=120.221 Z=0
    g167: Circle CenterX=175.022 CenterY=124.221 CenterZ=0 NormalX=0 NormalY=0 NormalZ=1 AngleXU=0 Radius=1
    g168: Circle CenterX=179.022 CenterY=124.221 CenterZ=0 NormalX=0 NormalY=0 NormalZ=1 AngleXU=0 Radius=1
    g169: Circle CenterX=179.022 CenterY=120.221 CenterZ=0 NormalX=0 NormalY=0 NormalZ=1 AngleXU=0 Radius=1
    g170: BSplineCurve PolesCount=3 KnotsCount=2 Degree=2 IsPeriodic=0
    g171: GeomPoint X=175.022 Y=124.221 Z=0
    g172: GeomPoint X=179.022 Y=120.221 Z=0
    g173: Circle CenterX=62.0728 CenterY=124.221 CenterZ=0 NormalX=0 NormalY=0 NormalZ=1 AngleXU=0 Radius=1
    g174: Circle CenterX=58.0728 CenterY=124.221 CenterZ=0 NormalX=0 NormalY=0 NormalZ=1 AngleXU=0 Radius=1
    g175: Circle CenterX=61.1496 CenterY=121.665 CenterZ=0 NormalX=0 NormalY=0 NormalZ=1 AngleXU=0 Radius=1
    g176: BSplineCurve PolesCount=3 KnotsCount=2 Degree=2 IsPeriodic=0
    g177: GeomPoint X=62.0728 Y=124.221 Z=0
    g178: GeomPoint X=61.1496 Y=121.665 Z=0
    g179: LineSegment StartX=62.0728 StartY=124.221 StartZ=0 EndX=175.022 EndY=124.221 EndZ=0
    g180: LineSegment StartX=179.022 StartY=120.221 StartZ=0 EndX=179.022 EndY=27.0628 EndZ=0
    g181: LineSegment StartX=185.124 StartY=27.0628 StartZ=0 EndX=185.124 EndY=120.221 EndZ=0
    g182: LineSegment StartX=302.996 StartY=121.665 StartZ=0 EndX=189.124 EndY=27.0628 EndZ=0
    g183: LineSegment StartX=175.022 StartY=27.0628 StartZ=0 EndX=61.1496 EndY=121.665 EndZ=0
    g184: Circle CenterX=61.5791 CenterY=75.4095 CenterZ=0 NormalX=0 NormalY=0 NormalZ=1 AngleXU=0 Radius=1
    g185: Circle CenterX=58.0728 CenterY=77.3346 CenterZ=0 NormalX=0 NormalY=0 NormalZ=1 AngleXU=0 Radius=1
    g186: Circle CenterX=58.0728 CenterY=73.3346 CenterZ=0 NormalX=0 NormalY=0 NormalZ=1 AngleXU=0 Radius=1
    g187: BSplineCurve PolesCount=3 KnotsCount=2 Degree=2 IsPeriodic=0
    g188: GeomPoint X=61.5791 Y=75.4095 Z=0
    g189: GeomPoint X=58.0728 Y=73.3346 Z=0
    g190: Circle CenterX=58.0728 CenterY=-40.8935 CenterZ=0 NormalX=0 NormalY=0 NormalZ=1 AngleXU=0 Radius=1
    g191: Circle CenterX=58.0728 CenterY=-44.8935 CenterZ=0 NormalX=0 NormalY=0 NormalZ=1 AngleXU=0 Radius=1
    g192: Circle CenterX=61.5791 CenterY=-42.9683 CenterZ=0 NormalX=0 NormalY=0 NormalZ=1 AngleXU=0 Radius=1
    g193: BSplineCurve PolesCount=3 KnotsCount=2 Degree=2 IsPeriodic=0
    g194: GeomPoint X=58.0728 Y=-40.8935 Z=0
    g195: GeomPoint X=61.5791 Y=-42.9683 Z=0
    g196: LineSegment StartX=61.5791 StartY=-42.9683 StartZ=0 EndX=165.871 EndY=14.2954 EndZ=0
    g197: LineSegment StartX=165.871 StartY=18.1458 StartZ=0 EndX=61.5791 EndY=75.4095 EndZ=0
    g198: LineSegment StartX=58.0728 StartY=73.3346 StartZ=0 EndX=58.0728 EndY=-40.8935 EndZ=0
    g199: Circle CenterX=302.567 CenterY=-42.9683 CenterZ=0 NormalX=0 NormalY=0 NormalZ=1 AngleXU=0 Radius=1
    g200: Circle CenterX=306.073 CenterY=-44.8935 CenterZ=0 NormalX=0 NormalY=0 NormalZ=1 AngleXU=0 Radius=1
    g201: Circle CenterX=306.073 CenterY=-40.8935 CenterZ=0 NormalX=0 NormalY=0 NormalZ=1 AngleXU=0 Radius=1
    g202: BSplineCurve PolesCount=3 KnotsCount=2 Degree=2 IsPeriodic=0
    g203: GeomPoint X=302.567 Y=-42.9683 Z=0
    g204: GeomPoint X=306.073 Y=-40.8935 Z=0
    g205: Circle CenterX=306.073 CenterY=73.3346 CenterZ=0 NormalX=0 NormalY=0 NormalZ=1 AngleXU=0 Radius=1
    g206: Circle CenterX=306.073 CenterY=77.3346 CenterZ=0 NormalX=0 NormalY=0 NormalZ=1 AngleXU=0 Radius=1
    g207: Circle CenterX=302.567 CenterY=75.4095 CenterZ=0 NormalX=0 NormalY=0 NormalZ=1 AngleXU=0 Radius=1
    g208: BSplineCurve PolesCount=3 KnotsCount=2 Degree=2 IsPeriodic=0
    g209: GeomPoint X=306.073 Y=73.3346 Z=0
    g210: GeomPoint X=302.567 Y=75.4095 Z=0
    g211: LineSegment StartX=302.567 StartY=-42.9683 StartZ=0 EndX=198.275 EndY=14.2954 EndZ=0
    g212: LineSegment StartX=198.275 StartY=18.1458 StartZ=0 EndX=302.567 EndY=75.4095 EndZ=0
    g213: LineSegment StartX=306.073 StartY=73.3346 StartZ=0 EndX=306.073 EndY=-40.8935 EndZ=0
    g214: LineSegment StartX=322.073 StartY=105.865 StartZ=0 EndX=328.643 EndY=105.865 EndZ=0
    g215: LineSegment StartX=318.073 StartY=120.221 StartZ=0 EndX=318.073 EndY=109.865 EndZ=0
    g216: LineSegment StartX=336.157 StartY=107.779 StartZ=0 EndX=362.567 EndY=122.294 EndZ=0
    g217: Circle CenterX=362.073 CenterY=124.221 CenterZ=0 NormalX=0 NormalY=0 NormalZ=1 AngleXU=0 Radius=1
    g218: Circle CenterX=366.073 CenterY=124.221 CenterZ=0 NormalX=0 NormalY=0 NormalZ=1 AngleXU=0 Radius=1
    g219: Circle CenterX=362.567 CenterY=122.294 CenterZ=0 NormalX=0 NormalY=0 NormalZ=1 AngleXU=0 Radius=1
    g220: BSplineCurve PolesCount=3 KnotsCount=2 Degree=2 IsPeriodic=0
    g221: GeomPoint X=362.073 Y=124.221 Z=0
    g222: GeomPoint X=362.567 Y=122.294 Z=0
    g223: Circle CenterX=322.073 CenterY=124.221 CenterZ=0 NormalX=0 NormalY=0 NormalZ=1 AngleXU=0 Radius=1
    g224: Circle CenterX=318.073 CenterY=124.221 CenterZ=0 NormalX=0 NormalY=0 NormalZ=1 AngleXU=0 Radius=1
    g225: Circle CenterX=318.073 CenterY=120.221 CenterZ=0 NormalX=0 NormalY=0 NormalZ=1 AngleXU=0 Radius=1
    g226: BSplineCurve PolesCount=3 KnotsCount=2 Degree=2 IsPeriodic=0
    g227: GeomPoint X=322.073 Y=124.221 Z=0
    g228: GeomPoint X=318.073 Y=120.221 Z=0
    g229: Circle CenterX=322.073 CenterY=105.865 CenterZ=0 NormalX=0 NormalY=0 NormalZ=1 AngleXU=0 Radius=1
    g230: Circle CenterX=318.073 CenterY=105.865 CenterZ=0 NormalX=0 NormalY=0 NormalZ=1 AngleXU=0 Radius=1
    g231: Circle CenterX=318.073 CenterY=109.865 CenterZ=0 NormalX=0 NormalY=0 NormalZ=1 AngleXU=0 Radius=1
    g232: BSplineCurve PolesCount=3 KnotsCount=2 Degree=2 IsPeriodic=0
    g233: GeomPoint X=322.073 Y=105.865 Z=0
    g234: GeomPoint X=318.073 Y=109.865 Z=0
    g235: Circle CenterX=336.157 CenterY=107.779 CenterZ=0 NormalX=0 NormalY=0 NormalZ=1 AngleXU=0 Radius=1
    g236: Circle CenterX=332.651 CenterY=105.853 CenterZ=0 NormalX=0 NormalY=0 NormalZ=1 AngleXU=0 Radius=1
    g237: Circle CenterX=328.643 CenterY=105.865 CenterZ=0 NormalX=0 NormalY=0 NormalZ=1 AngleXU=0 Radius=1
    g238: BSplineCurve PolesCount=3 KnotsCount=2 Degree=2 IsPeriodic=0
    g239: GeomPoint X=336.157 Y=107.779 Z=0
    g240: GeomPoint X=328.643 Y=105.865 Z=0
    g241: LineSegment StartX=322.073 StartY=124.221 StartZ=0 EndX=362.073 EndY=124.221 EndZ=0
    g242: Circle CenterX=371.567 CenterY=-80.8644 CenterZ=0 NormalX=0 NormalY=0 NormalZ=1 AngleXU=0 Radius=1
    g243: Circle CenterX=375.073 CenterY=-82.7896 CenterZ=0 NormalX=0 NormalY=0 NormalZ=1 AngleXU=0 Radius=1
    g244: Circle CenterX=375.073 CenterY=-78.7896 CenterZ=0 NormalX=0 NormalY=0 NormalZ=1 AngleXU=0 Radius=1
    g245: BSplineCurve PolesCount=3 KnotsCount=2 Degree=2 IsPeriodic=0
    g246: GeomPoint X=371.567 Y=-80.8644 Z=0
    g247: GeomPoint X=375.073 Y=-78.7896 Z=0
    g248: Circle CenterX=321.579 CenterY=-53.4075 CenterZ=0 NormalX=0 NormalY=0 NormalZ=1 AngleXU=0 Radius=1
    g249: Circle CenterX=318.073 CenterY=-51.4823 CenterZ=0 NormalX=0 NormalY=0 NormalZ=1 AngleXU=0 Radius=1
    g250: Circle CenterX=318.073 CenterY=-47.4805 CenterZ=0 NormalX=0 NormalY=0 NormalZ=1 AngleXU=0 Radius=1
    g251: BSplineCurve PolesCount=3 KnotsCount=2 Degree=2 IsPeriodic=0
    g252: GeomPoint X=321.579 Y=-53.4075 Z=0
    g253: GeomPoint X=318.073 Y=-47.4805 Z=0
    g254: LineSegment StartX=371.567 StartY=-80.8644 StartZ=0 EndX=321.579 EndY=-53.4075 EndZ=0
    g255: Circle CenterX=321.579 CenterY=-67.3492 CenterZ=0 NormalX=0 NormalY=0 NormalZ=1 AngleXU=0 Radius=1
    g256: Circle CenterX=318.073 CenterY=-65.424 CenterZ=0 NormalX=0 NormalY=0 NormalZ=1 AngleXU=0 Radius=1
    g257: Circle CenterX=318.073 CenterY=-69.424 CenterZ=0 NormalX=0 NormalY=0 NormalZ=1 AngleXU=0 Radius=1
    g258: BSplineCurve PolesCount=3 KnotsCount=2 Degree=2 IsPeriodic=0
    g259: GeomPoint X=321.579 Y=-67.3492 Z=0
    g260: GeomPoint X=318.073 Y=-69.424 Z=0
    g261: Circle CenterX=362.567 CenterY=-89.8542 CenterZ=0 NormalX=0 NormalY=0 NormalZ=1 AngleXU=0 Radius=1
    g262: Circle CenterX=366.073 CenterY=-91.7794 CenterZ=0 NormalX=0 NormalY=0 NormalZ=1 AngleXU=0 Radius=1
    g263: Circle CenterX=362.073 CenterY=-91.7794 CenterZ=0 NormalX=0 NormalY=0 NormalZ=1 AngleXU=0 Radius=1
    g264: BSplineCurve PolesCount=3 KnotsCount=2 Degree=2 IsPeriodic=0
    g265: GeomPoint X=362.567 Y=-89.8542 Z=0
    g266: GeomPoint X=362.073 Y=-91.7794 Z=0
    g267: Circle CenterX=322.073 CenterY=-91.7794 CenterZ=0 NormalX=0 NormalY=0 NormalZ=1 AngleXU=0 Radius=1
    g268: Circle CenterX=318.073 CenterY=-91.7794 CenterZ=0 NormalX=0 NormalY=0 NormalZ=1 AngleXU=0 Radius=1
    g269: Circle CenterX=318.073 CenterY=-87.7794 CenterZ=0 NormalX=0 NormalY=0 NormalZ=1 AngleXU=0 Radius=1
    g270: BSplineCurve PolesCount=3 KnotsCount=2 Degree=2 IsPeriodic=0
    g271: GeomPoint X=322.073 Y=-91.7794 Z=0
    g272: GeomPoint X=318.073 Y=-87.7794 Z=0
    g273: LineSegment StartX=362.567 StartY=-89.8542 StartZ=0 EndX=321.579 EndY=-67.3492 EndZ=0
    g274: LineSegment StartX=318.073 StartY=-69.424 StartZ=0 EndX=318.073 EndY=-87.7794 EndZ=0
    g275: LineSegment StartX=322.073 StartY=-91.7794 StartZ=0 EndX=362.073 EndY=-91.7794 EndZ=0
    g276: Circle CenterX=2.07281 CenterY=124.221 CenterZ=0 NormalX=0 NormalY=0 NormalZ=1 AngleXU=0 Radius=1
    g277: Circle CenterX=1.57905 CenterY=122.295 CenterZ=0 NormalX=0 NormalY=0 NormalZ=1 AngleXU=0 Radius=1
    g278: BSplineCurve PolesCount=3 KnotsCount=2 Degree=2 IsPeriodic=0
    g279: GeomPoint X=2.07281 Y=124.221 Z=0
    g280: GeomPoint X=1.57905 Y=122.295 Z=0
    g281: Circle CenterX=42.0728 CenterY=124.221 CenterZ=0 NormalX=0 NormalY=0 NormalZ=1 AngleXU=0 Radius=1
    g282: Circle CenterX=46.0728 CenterY=124.221 CenterZ=0 NormalX=0 NormalY=0 NormalZ=1 AngleXU=0 Radius=1
    g283: Circle CenterX=46.0728 CenterY=120.221 CenterZ=0 NormalX=0 NormalY=0 NormalZ=1 AngleXU=0 Radius=1
    g284: BSplineCurve PolesCount=3 KnotsCount=2 Degree=2 IsPeriodic=0
    g285: GeomPoint X=42.0728 Y=124.221 Z=0
    g286: GeomPoint X=46.0728 Y=120.221 Z=0
    g287: Circle CenterX=46.0728 CenterY=109.865 CenterZ=0 NormalX=0 NormalY=0 NormalZ=1 AngleXU=0 Radius=1
    g288: Circle CenterX=46.0728 CenterY=105.865 CenterZ=0 NormalX=0 NormalY=0 NormalZ=1 AngleXU=0 Radius=1
    g289: Circle CenterX=42.0728 CenterY=105.865 CenterZ=0 NormalX=0 NormalY=0 NormalZ=1 AngleXU=0 Radius=1
    g290: BSplineCurve PolesCount=3 KnotsCount=2 Degree=2 IsPeriodic=0
    g291: GeomPoint X=46.0728 Y=109.865 Z=0
    g292: GeomPoint X=42.0728 Y=105.865 Z=0
    g293: Circle CenterX=35.5028 CenterY=105.865 CenterZ=0 NormalX=0 NormalY=0 NormalZ=1 AngleXU=0 Radius=1
    g294: Circle CenterX=31.5028 CenterY=105.865 CenterZ=0 NormalX=0 NormalY=0 NormalZ=1 AngleXU=0 Radius=1
    g295: Circle CenterX=27.9965 CenterY=107.79 CenterZ=0 NormalX=0 NormalY=0 NormalZ=1 AngleXU=0 Radius=1
    g296: BSplineCurve PolesCount=3 KnotsCount=2 Degree=2 IsPeriodic=0
    g297: GeomPoint X=35.5028 Y=105.865 Z=0
    g298: GeomPoint X=27.9965 Y=107.79 Z=0
    g299: LineSegment StartX=2.07281 StartY=124.221 StartZ=0 EndX=42.0728 EndY=124.221 EndZ=0
    g300: LineSegment StartX=46.0728 StartY=120.221 StartZ=0 EndX=46.0728 EndY=109.865 EndZ=0
    g301: LineSegment StartX=42.0728 StartY=105.865 StartZ=0 EndX=35.5028 EndY=105.865 EndZ=0
    g302: LineSegment StartX=27.9965 StartY=107.79 StartZ=0 EndX=1.57905 EndY=122.295 EndZ=0
    g303: Circle CenterX=42.5666 CenterY=-67.3492 CenterZ=0 NormalX=0 NormalY=0 NormalZ=1 AngleXU=0 Radius=1
    g304: Circle CenterX=46.0728 CenterY=-65.424 CenterZ=0 NormalX=0 NormalY=0 NormalZ=1 AngleXU=0 Radius=1
    g305: Circle CenterX=46.0728 CenterY=-69.424 CenterZ=0 NormalX=0 NormalY=0 NormalZ=1 AngleXU=0 Radius=1
    g306: BSplineCurve PolesCount=3 KnotsCount=2 Degree=2 IsPeriodic=0
    g307: GeomPoint X=42.5666 Y=-67.3492 Z=0
    g308: GeomPoint X=46.0728 Y=-69.424 Z=0
    g309: Circle CenterX=46.0728 CenterY=-87.7794 CenterZ=0 NormalX=0 NormalY=0 NormalZ=1 AngleXU=0 Radius=1
    g310: Circle CenterX=46.0728 CenterY=-91.7794 CenterZ=0 NormalX=0 NormalY=0 NormalZ=1 AngleXU=0 Radius=1
    g311: Circle CenterX=42.0728 CenterY=-91.7794 CenterZ=0 NormalX=0 NormalY=0 NormalZ=1 AngleXU=0 Radius=1
    g312: BSplineCurve PolesCount=3 KnotsCount=2 Degree=2 IsPeriodic=0
    g313: GeomPoint X=46.0728 Y=-87.7794 Z=0
    g314: GeomPoint X=42.0728 Y=-91.7794 Z=0
    g315: Circle CenterX=2.07281 CenterY=-91.7794 CenterZ=0 NormalX=0 NormalY=0 NormalZ=1 AngleXU=0 Radius=1
    g316: Circle CenterX=-1.92719 CenterY=-91.7794 CenterZ=0 NormalX=0 NormalY=0 NormalZ=1 AngleXU=0 Radius=1
    g317: Circle CenterX=1.57905 CenterY=-89.8542 CenterZ=0 NormalX=0 NormalY=0 NormalZ=1 AngleXU=0 Radius=1
    g318: BSplineCurve PolesCount=3 KnotsCount=2 Degree=2 IsPeriodic=0
    g319: GeomPoint X=2.07281 Y=-91.7794 Z=0
    g320: GeomPoint X=1.57905 Y=-89.8542 Z=0
    g321: LineSegment StartX=2.07281 StartY=-91.7794 StartZ=0 EndX=42.0728 EndY=-91.7794 EndZ=0
    g322: LineSegment StartX=46.0728 StartY=-87.7794 StartZ=0 EndX=46.0728 EndY=-69.424 EndZ=0
    g323: LineSegment StartX=42.5666 StartY=-67.3492 StartZ=0 EndX=1.57905 EndY=-89.8542 EndZ=0
    g324: Circle CenterX=322.073 CenterY=76.4095 CenterZ=0 NormalX=0 NormalY=0 NormalZ=1 AngleXU=0 Radius=4
    g325: BSplineCurve PolesCount=3 KnotsCount=2 Degree=2 IsPeriodic=0
    g326: GeomPoint X=318.073 Y=72.4095 Z=0
    g327: GeomPoint X=322.073 Y=76.4095 Z=0
    g328: Circle CenterX=375.073 CenterY=72.4095 CenterZ=0 NormalX=0 NormalY=0 NormalZ=1 AngleXU=0 Radius=1
    g329: Circle CenterX=375.073 CenterY=76.4095 CenterZ=0 NormalX=0 NormalY=0 NormalZ=1 AngleXU=0 Radius=1
    g330: Circle CenterX=371.073 CenterY=76.4095 CenterZ=0 NormalX=0 NormalY=0 NormalZ=1 AngleXU=0 Radius=1
    g331: BSplineCurve PolesCount=3 KnotsCount=2 Degree=2 IsPeriodic=0
    g332: GeomPoint X=375.073 Y=72.4095 Z=0
    g333: GeomPoint X=371.073 Y=76.4095 Z=0
    g334: LineSegment StartX=322.073 StartY=76.4095 StartZ=0 EndX=371.073 EndY=76.4095 EndZ=0
    g335: LineSegment StartX=318.073 StartY=72.4095 StartZ=0 EndX=318.073 EndY=-47.4805 EndZ=0
    g336: LineSegment StartX=375.073 StartY=72.4095 StartZ=0 EndX=375.073 EndY=-78.7896 EndZ=0
    g337: ArcOfCircle CenterX=-26.9272 CenterY=22.1087 CenterZ=0 NormalX=0 NormalY=0 NormalZ=1 AngleXU=0 Radius=4 StartAngle=5e-16 EndAngle=3.14159
    g338: LineSegment StartX=-22.9272 StartY=22.1087 StartZ=0 EndX=-18.9272 EndY=-83.7794 EndZ=0
    g339: LineSegment StartX=-34.9272 StartY=-83.7794 StartZ=0 EndX=-30.9272 EndY=22.1087 EndZ=0
    g340: ArcOfCircle CenterX=391.073 CenterY=22.1087 CenterZ=0 NormalX=0 NormalY=0 NormalZ=1 AngleXU=0 Radius=4 StartAngle=0 EndAngle=3.14159
    g341: LineSegment StartX=387.073 StartY=22.1087 StartZ=0 EndX=383.073 EndY=-83.7794 EndZ=0
    g342: LineSegment StartX=395.073 StartY=22.1087 StartZ=0 EndX=399.073 EndY=-83.7794 EndZ=0
    g343: Circle CenterX=-10.9272 CenterY=-78.7794 CenterZ=0 NormalX=0 NormalY=0 NormalZ=1 AngleXU=0 Radius=1
    g344: Circle CenterX=-10.9272 CenterY=-82.7794 CenterZ=0 NormalX=0 NormalY=0 NormalZ=1 AngleXU=0 Radius=1
    g345: Circle CenterX=-7.42095 CenterY=-80.8542 CenterZ=0 NormalX=0 NormalY=0 NormalZ=1 AngleXU=0 Radius=1
    g346: BSplineCurve PolesCount=3 KnotsCount=2 Degree=2 IsPeriodic=0
    g347: GeomPoint X=-10.9272 Y=-78.7794 Z=0
    g348: GeomPoint X=-7.42095 Y=-80.8542 Z=0
    g349: Circle CenterX=42.5666 CenterY=-53.4075 CenterZ=0 NormalX=0 NormalY=0 NormalZ=1 AngleXU=0 Radius=1
    g350: Circle CenterX=46.0728 CenterY=-51.4823 CenterZ=0 NormalX=0 NormalY=0 NormalZ=1 AngleXU=0 Radius=1
    g351: Circle CenterX=46.0728 CenterY=-47.4823 CenterZ=0 NormalX=0 NormalY=0 NormalZ=1 AngleXU=0 Radius=1
    g352: BSplineCurve PolesCount=3 KnotsCount=2 Degree=2 IsPeriodic=0
    g353: GeomPoint X=42.5666 Y=-53.4075 Z=0
    g354: GeomPoint X=46.0728 Y=-47.4823 Z=0
    g355: Circle CenterX=46.0728 CenterY=72.4095 CenterZ=0 NormalX=0 NormalY=0 NormalZ=1 AngleXU=0 Radius=1
    g356: Circle CenterX=46.0728 CenterY=76.4095 CenterZ=0 NormalX=0 NormalY=0 NormalZ=1 AngleXU=0 Radius=1
    g357: Circle CenterX=42.0728 CenterY=76.4095 CenterZ=0 NormalX=0 NormalY=0 NormalZ=1 AngleXU=0 Radius=1
    g358: BSplineCurve PolesCount=3 KnotsCount=2 Degree=2 IsPeriodic=0
    g359: GeomPoint X=46.0728 Y=72.4095 Z=0
    g360: GeomPoint X=42.0728 Y=76.4095 Z=0
    g361: Circle CenterX=-6.92718 CenterY=76.4095 CenterZ=0 NormalX=0 NormalY=0 NormalZ=1 AngleXU=0 Radius=1
    g362: Circle CenterX=-10.9272 CenterY=76.4095 CenterZ=0 NormalX=0 NormalY=0 NormalZ=1 AngleXU=0 Radius=1
    g363: Circle CenterX=-10.9272 CenterY=72.4095 CenterZ=0 NormalX=0 NormalY=0 NormalZ=1 AngleXU=0 Radius=1
    g364: BSplineCurve PolesCount=3 KnotsCount=2 Degree=2 IsPeriodic=0
    g365: GeomPoint X=-6.92718 Y=76.4095 Z=0
    g366: GeomPoint X=-10.9272 Y=72.4095 Z=0
    g367: LineSegment StartX=-10.9272 StartY=72.4095 StartZ=0 EndX=-10.9272 EndY=-78.7794 EndZ=0
    g368: LineSegment StartX=-7.42095 StartY=-80.8542 StartZ=0 EndX=42.5666 EndY=-53.4075 EndZ=0
    g369: LineSegment StartX=46.0728 StartY=-47.4823 StartZ=0 EndX=46.0728 EndY=72.4095 EndZ=0
    g370: LineSegment StartX=42.0728 StartY=76.4095 StartZ=0 EndX=-6.92719 EndY=76.4095 EndZ=0
    g371: LineSegment StartX=232.072 StartY=136.221 StartZ=0 EndX=232.072 EndY=-117.815 EndZ=0
    g372: LineSegment StartX=132.072 StartY=136.221 StartZ=0 EndX=132.072 EndY=-121.309 EndZ=0
    g373: LineSegment StartX=245.072 StartY=136.221 StartZ=0 EndX=245.072 EndY=-116.499 EndZ=0
    g374: LineSegment StartX=119.072 StartY=136.221 StartZ=0 EndX=119.072 EndY=-116.228 EndZ=0
    g375: LineSegment StartX=-42.9272 StartY=136.221 StartZ=0 EndX=407.073 EndY=136.221 EndZ=0
    g376: LineSegment StartX=232.072 StartY=136.221 StartZ=0 EndX=220.072 EndY=136.221 EndZ=0
    g377: LineSegment StartX=232.072 StartY=136.221 StartZ=0 EndX=232.072 EndY=124.221 EndZ=0
    g378: LineSegment StartX=220.072 StartY=136.221 StartZ=0 EndX=220.072 EndY=124.221 EndZ=0
    g379: LineSegment StartX=220.072 StartY=136.221 StartZ=0 EndX=226.072 EndY=136.221 EndZ=0
    g380: LineSegment StartX=220.072 StartY=136.221 StartZ=0 EndX=220.072 EndY=130.221 EndZ=0
    g381: LineSegment StartX=220.072 StartY=124.221 StartZ=0 EndX=226.072 EndY=124.221 EndZ=0
    g382: LineSegment StartX=232.072 StartY=124.221 StartZ=0 EndX=232.072 EndY=127.221 EndZ=0
    g383: LineSegment StartX=232.072 StartY=136.221 StartZ=0 EndX=232.072 EndY=133.221 EndZ=0
    g384-g388: Circle x5 (B-spline internal-alignment scaffolding for g389; pole/knot coordinates omitted)
    g389: BSplineCurve PolesCount=5 KnotsCount=3 Degree=3 IsPeriodic=0
    g390: GeomPoint X=232.072 Y=133.221 Z=0
    g391: GeomPoint X=223.072 Y=130.221 Z=0
    g392: GeomPoint X=232.072 Y=127.221 Z=0
    g393: LineSegment StartX=189.124 StartY=124.221 StartZ=0 EndX=302.073 EndY=124.221 EndZ=0
    g394: LineSegment StartX=132.635 StartY=124.947 StartZ=0 EndX=145.61 EndY=124.947 EndZ=0
  constraints (663):
    c: Vertical(g0)
    c: Vertical(g1)
    c: Block(g1)
    c: Block(g0)
    c: Weight(g4) = 1
    c: Equal(g4,g5)
    c: Equal(g4,g6)
    c: InternalAlignment(g4,g7)
    c: InternalAlignment(g5,g7)
    c: InternalAlignment(g6,g7)
    c: InternalAlignment(g8,g7)
    c: InternalAlignment(g9,g7)
    c: Weight(g10) = 1
    c: Equal(g10,g11)
    c: Equal(g10,g12)
    c: InternalAlignment(g10,g13)
    c: InternalAlignment(g11,g13)
    c: InternalAlignment(g12,g13)
    c: InternalAlignment(g14,g13)
    c: InternalAlignment(g15,g13)
    c: Block(g13)
    c: Block(g7)
    c: Weight(g16) = 1
    c: Equal(g16,g17)
    c: Equal(g16,g18)
    c: InternalAlignment(g16,g19)
    c: InternalAlignment(g17,g19)
    c: InternalAlignment(g18,g19)
    c: InternalAlignment(g20,g19)
    c: InternalAlignment(g21,g19)
    c: Weight(g22) = 1
    c: Equal(g22,g23)
    c: Equal(g22,g24)
    c: InternalAlignment(g22,g25)
    c: InternalAlignment(g23,g25)
    c: InternalAlignment(g24,g25)
    c: InternalAlignment(g26,g25)
    c: InternalAlignment(g27,g25)
    c: Block(g25)
    c: Block(g19)
    c: Weight(g28) = 1
    c: Equal(g28,g29)
    c: Equal(g28,g30)
    c: InternalAlignment(g28,g31)
    c: InternalAlignment(g29,g31)
    c: InternalAlignment(g30,g31)
    c: InternalAlignment(g32,g31)
    c: InternalAlignment(g33,g31)
    c: Weight(g34) = 1
    c: Equal(g34,g35)
    c: Equal(g34,g36)
    c: InternalAlignment(g34,g37)
    c: InternalAlignment(g35,g37)
    c: InternalAlignment(g36,g37)
    c: InternalAlignment(g38,g37)
    c: InternalAlignment(g39,g37)
    c: Block(g31)
    c: Block(g37)
    c: Coincident(g40,g1)
    c: Coincident(g40,g0)
    c: Horizontal(g40)
    c: Distance(g40) = 450
    c: Weight(g41) = 1
    c: Equal(g41,g42)
    c: Equal(g41,g43)
    c: InternalAlignment(g41,g44)
    c: InternalAlignment(g42,g44)
    c: InternalAlignment(g43,g44)
    c: InternalAlignment(g45,g44)
    c: InternalAlignment(g46,g44)
    c: Block(g44)
    c: Weight(g47) = 1
    c: Equal(g47,g48)
    c: Equal(g47,g49)
    c: InternalAlignment(g47,g50)
    c: InternalAlignment(g48,g50)
    c: InternalAlignment(g49,g50)
    c: InternalAlignment(g51,g50)
    c: InternalAlignment(g52,g50)
    c: Block(g50)
    c: Weight(g53) = 1
    c: Equal(g53,g54)
    c: Equal(g53,g55)
    c: InternalAlignment(g53,g56)
    c: InternalAlignment(g54,g56)
    c: InternalAlignment(g55,g56)
    c: InternalAlignment(g57,g56)
    c: InternalAlignment(g58,g56)
    c: Block(g56)
    c: Weight(g59) = 1
    c: Equal(g59,g60)
    c: Equal(g59,g61)
    c: InternalAlignment(g59,g62)
    c: InternalAlignment(g60,g62)
    c: InternalAlignment(g61,g62)
    c: InternalAlignment(g63,g62)
    c: InternalAlignment(g64,g62)
    c: Block(g62)
    c: Weight(g65) = 1
    c: Equal(g65,g66)
    c: Equal(g65,g67)
    c: InternalAlignment(g65,g68)
    c: InternalAlignment(g66,g68)
    c: InternalAlignment(g67,g68)
    c: InternalAlignment(g69,g68)
    c: InternalAlignment(g70,g68)
    c: Weight(g71) = 1
    c: Equal(g71,g72)
    c: Equal(g71,g73)
    c: InternalAlignment(g71,g74)
    c: InternalAlignment(g72,g74)
    c: InternalAlignment(g73,g74)
    c: InternalAlignment(g75,g74)
    c: InternalAlignment(g76,g74)
    c: Block(g68)
    c: Block(g74)
    c: Coincident(g77,g68)
    c: Coincident(g77,g74)
    c: Vertical(g77)
    c: Coincident(g78,g68)
    c: Coincident(g78,g50)
    c: Coincident(g79,g50)
    c: Coincident(g79,g74)
    c: Weight(g80) = 1
    c: Equal(g80,g81)
    c: Equal(g80,g82)
    c: InternalAlignment(g80,g83)
    c: InternalAlignment(g81,g83)
    c: InternalAlignment(g82,g83)
    c: InternalAlignment(g84,g83)
    c: InternalAlignment(g85,g83)
    c: Weight(g86) = 1
    c: Equal(g86,g87)
    c: Equal(g86,g88)
    c: InternalAlignment(g86,g89)
    c: InternalAlignment(g87,g89)
    c: InternalAlignment(g88,g89)
    c: InternalAlignment(g90,g89)
    c: InternalAlignment(g91,g89)
    c: Block(g83)
    c: Block(g89)
    c: Coincident(g92,g83)
    c: Coincident(g92,g89)
    c: Vertical(g92)
    c: Coincident(g93,g83)
    c: Coincident(g93,g44)
    c: Coincident(g94,g44)
    c: Coincident(g94,g89)
    c: Weight(g95) = 1
    c: Equal(g95,g96)
    c: Equal(g95,g97)
    c: InternalAlignment(g95,g98)
    c: InternalAlignment(g96,g98)
    c: InternalAlignment(g97,g98)
    c: InternalAlignment(g99,g98)
    c: InternalAlignment(g100,g98)
    c: Weight(g101) = 1
    c: Equal(g101,g102)
    c: Equal(g101,g103)
    c: InternalAlignment(g101,g104)
    c: InternalAlignment(g102,g104)
    c: InternalAlignment(g103,g104)
    c: InternalAlignment(g105,g104)
    c: InternalAlignment(g106,g104)
    c: Block(g98)
    c: Block(g104)
    c: Coincident(g107,g98)
    c: Coincident(g107,g104)
    c: Vertical(g107)
    c: Coincident(g108,g104)
    c: Coincident(g108,g62)
    c: Coincident(g109,g62)
    c: Coincident(g109,g98)
    c: Weight(g110) = 1
    c: Equal(g110,g111)
    c: Equal(g110,g112)
    c: InternalAlignment(g110,g113)
    c: InternalAlignment(g111,g113)
    c: InternalAlignment(g112,g113)
    c: InternalAlignment(g114,g113)
    c: InternalAlignment(g115,g113)
    c: Weight(g116) = 1
    c: Equal(g116,g117)
    c: Equal(g116,g118)
    c: InternalAlignment(g116,g119)
    c: InternalAlignment(g117,g119)
    c: InternalAlignment(g118,g119)
    c: InternalAlignment(g120,g119)
    c: InternalAlignment(g121,g119)
    c: Block(g113)
    c: Block(g119)
    c: Coincident(g122,g113)
    c: Coincident(g122,g119)
    c: Vertical(g122)
    c: Coincident(g123,g119)
    c: Coincident(g123,g56)
    c: Coincident(g124,g56)
    c: Coincident(g124,g113)
    c: Weight(g125) = 1
    c: Equal(g125,g126)
    c: Equal(g125,g127)
    c: InternalAlignment(g125,g128)
    c: InternalAlignment(g126,g128)
    c: InternalAlignment(g127,g128)
    c: InternalAlignment(g129,g128)
    c: InternalAlignment(g130,g128)
    c: Weight(g131) = 1
    c: Equal(g131,g132)
    c: Equal(g131,g133)
    c: InternalAlignment(g131,g134)
    c: InternalAlignment(g132,g134)
    c: InternalAlignment(g133,g134)
    c: InternalAlignment(g135,g134)
    c: InternalAlignment(g136,g134)
    c: Weight(g137) = 1
    c: Equal(g137,g138)
    c: Equal(g137,g139)
    c: InternalAlignment(g137,g140)
    c: InternalAlignment(g138,g140)
    c: InternalAlignment(g139,g140)
    c: InternalAlignment(g141,g140)
    c: InternalAlignment(g142,g140)
    c: Weight(g143) = 1
    c: Equal(g143,g144)
    c: Equal(g143,g145)
    c: InternalAlignment(g143,g146)
    c: InternalAlignment(g144,g146)
    c: InternalAlignment(g145,g146)
    c: InternalAlignment(g147,g146)
    c: InternalAlignment(g148,g146)
    c: Block(g146)
    c: Block(g140)
    c: Block(g134)
    c: Block(g128)
    c: Coincident(g149,g25)
    c: Coincident(g149,g146)
    c: Coincident(g150,g146)
    c: Coincident(g150,g140)
    c: Horizontal(g150)
    c: Coincident(g151,g140)
    c: Coincident(g151,g25)
    c: Vertical(g151)
    c: Coincident(g152,g19)
    c: Coincident(g152,g134)
    c: Vertical(g152)
    c: Coincident(g153,g134)
    c: Coincident(g153,g128)
    c: Horizontal(g153)
    c: Coincident(g154,g128)
    c: Coincident(g154,g19)
    c: Weight(g155) = 1
    c: Equal(g155,g156)
    c: Equal(g155,g157)
    c: InternalAlignment(g155,g158)
    c: InternalAlignment(g156,g158)
    c: InternalAlignment(g157,g158)
    c: InternalAlignment(g159,g158)
    c: InternalAlignment(g160,g158)
    c: Weight(g161) = 1
    c: Equal(g161,g162)
    c: Equal(g161,g163)
    c: InternalAlignment(g161,g164)
    c: InternalAlignment(g162,g164)
    c: InternalAlignment(g163,g164)
    c: InternalAlignment(g165,g164)
    c: InternalAlignment(g166,g164)
    c: Weight(g167) = 1
    c: Equal(g167,g168)
    c: Equal(g167,g169)
    c: InternalAlignment(g167,g170)
    c: InternalAlignment(g168,g170)
    c: InternalAlignment(g169,g170)
    c: InternalAlignment(g171,g170)
    c: InternalAlignment(g172,g170)
    c: Weight(g173) = 1
    c: Equal(g173,g174)
    c: Equal(g173,g175)
    c: InternalAlignment(g173,g176)
    c: InternalAlignment(g174,g176)
    c: InternalAlignment(g175,g176)
    c: InternalAlignment(g177,g176)
    c: InternalAlignment(g178,g176)
    c: Block(g176)
    c: Block(g170)
    c: Block(g164)
    c: Block(g158)
    c: Coincident(g179,g176)
    c: Coincident(g179,g170)
    c: Horizontal(g179)
    c: Coincident(g180,g170)
    c: Coincident(g180,g7)
    c: Vertical(g180)
    c: Coincident(g181,g13)
    c: Coincident(g181,g164)
    c: Vertical(g181)
    c: Coincident(g182,g158)
    c: Coincident(g182,g13)
    c: Coincident(g183,g7)
    c: Weight(g184) = 1
    c: Equal(g184,g185)
    c: Equal(g184,g186)
    c: InternalAlignment(g184,g187)
    c: InternalAlignment(g185,g187)
    c: InternalAlignment(g186,g187)
    c: InternalAlignment(g188,g187)
    c: InternalAlignment(g189,g187)
    c: Weight(g190) = 1
    c: Equal(g190,g191)
    c: Equal(g190,g192)
    c: InternalAlignment(g190,g193)
    c: InternalAlignment(g191,g193)
    c: InternalAlignment(g192,g193)
    c: InternalAlignment(g194,g193)
    c: InternalAlignment(g195,g193)
    c: Block(g193)
    c: Block(g187)
    c: Coincident(g196,g193)
    c: Coincident(g196,g31)
    c: Coincident(g197,g31)
    c: Coincident(g197,g187)
    c: Coincident(g198,g187)
    c: Coincident(g198,g193)
    c: Vertical(g198)
    c: Weight(g199) = 1
    c: Equal(g199,g200)
    c: Equal(g199,g201)
    c: InternalAlignment(g199,g202)
    c: InternalAlignment(g200,g202)
    c: InternalAlignment(g201,g202)
    c: InternalAlignment(g203,g202)
    c: InternalAlignment(g204,g202)
    c: Weight(g205) = 1
    c: Equal(g205,g206)
    c: Equal(g205,g207)
    c: InternalAlignment(g205,g208)
    c: InternalAlignment(g206,g208)
    c: InternalAlignment(g207,g208)
    c: InternalAlignment(g209,g208)
    c: InternalAlignment(g210,g208)
    c: Block(g208)
    c: Block(g202)
    c: Coincident(g211,g202)
    c: Coincident(g211,g37)
    c: Coincident(g212,g37)
    c: Coincident(g212,g208)
    c: Coincident(g213,g208)
    c: Coincident(g213,g202)
    c: Vertical(g213)
    c: Horizontal(g214)
    c: Block(g214)
    c: Vertical(g215)
    c: Block(g215)
    c: Block(g216)
    c: Weight(g217) = 1
    c: Equal(g217,g218)
    c: Equal(g217,g219)
    c: InternalAlignment(g217,g220)
    c: InternalAlignment(g218,g220)
    c: InternalAlignment(g219,g220)
    c: InternalAlignment(g221,g220)
    c: InternalAlignment(g222,g220)
    c: Weight(g223) = 1
    c: Equal(g223,g224)
    c: Equal(g223,g225)
    c: InternalAlignment(g223,g226)
    c: InternalAlignment(g224,g226)
    c: InternalAlignment(g225,g226)
    c: InternalAlignment(g227,g226)
    c: InternalAlignment(g228,g226)
    c: Weight(g229) = 1
    c: Equal(g229,g230)
    c: Equal(g229,g231)
    c: InternalAlignment(g229,g232)
    c: InternalAlignment(g230,g232)
    c: InternalAlignment(g231,g232)
    c: InternalAlignment(g233,g232)
    c: InternalAlignment(g234,g232)
    c: Weight(g235) = 1
    c: Equal(g235,g236)
    c: Equal(g235,g237)
    c: InternalAlignment(g235,g238)
    c: InternalAlignment(g236,g238)
    c: InternalAlignment(g237,g238)
    c: InternalAlignment(g239,g238)
    c: InternalAlignment(g240,g238)
    c: Block(g220)
    c: Block(g226)
    c: Block(g232)
    c: Block(g238)
    c: Coincident(g241,g226)
    c: Coincident(g241,g220)
    c: Horizontal(g241)
    c: Block(g183)
    c: Weight(g242) = 1
    c: Equal(g242,g243)
    c: Equal(g242,g244)
    c: InternalAlignment(g242,g245)
    c: InternalAlignment(g243,g245)
    c: InternalAlignment(g244,g245)
    c: InternalAlignment(g246,g245)
    c: InternalAlignment(g247,g245)
    c: Weight(g248) = 1
    c: Equal(g248,g249)
    c: Equal(g248,g250)
    c: InternalAlignment(g248,g251)
    c: InternalAlignment(g249,g251)
    c: InternalAlignment(g250,g251)
    c: InternalAlignment(g252,g251)
    c: InternalAlignment(g253,g251)
    c: Block(g245)
    c: Block(g251)
    c: Coincident(g254,g245)
    c: Coincident(g254,g251)
    c: Weight(g255) = 1
    c: Equal(g255,g256)
    c: Equal(g255,g257)
    c: InternalAlignment(g255,g258)
    c: InternalAlignment(g256,g258)
    c: InternalAlignment(g257,g258)
    c: InternalAlignment(g259,g258)
    c: InternalAlignment(g260,g258)
    c: Weight(g261) = 1
    c: Equal(g261,g262)
    c: Equal(g261,g263)
    c: InternalAlignment(g261,g264)
    c: InternalAlignment(g262,g264)
    c: InternalAlignment(g263,g264)
    c: InternalAlignment(g265,g264)
    c: InternalAlignment(g266,g264)
    c: Weight(g267) = 1
    c: Equal(g267,g268)
    c: Equal(g267,g269)
    c: InternalAlignment(g267,g270)
    c: InternalAlignment(g268,g270)
    c: InternalAlignment(g269,g270)
    c: InternalAlignment(g271,g270)
    c: InternalAlignment(g272,g270)
    c: Block(g270)
    c: Block(g264)
    c: Block(g258)
    c: Coincident(g273,g264)
    c: Coincident(g273,g258)
    c: Coincident(g274,g258)
    c: Coincident(g274,g270)
    c: Vertical(g274)
    c: Coincident(g275,g270)
    c: Coincident(g275,g264)
    c: Horizontal(g275)
    c: Weight(g276) = 1
    c: Equal(g276,g277)
    c: InternalAlignment(g276,g278)
    c: InternalAlignment(g277,g278)
    c: InternalAlignment(g279,g278)
    c: InternalAlignment(g280,g278)
    c: Weight(g281) = 1
    c: InternalAlignment(g282,g284)
    c: InternalAlignment(g283,g284)
    c: InternalAlignment(g285,g284)
    c: InternalAlignment(g286,g284)
    c: Weight(g287) = 1
    c: Equal(g287,g288)
    c: Equal(g287,g289)
    c: InternalAlignment(g287,g290)
    c: InternalAlignment(g288,g290)
    c: InternalAlignment(g289,g290)
    c: InternalAlignment(g291,g290)
    c: InternalAlignment(g292,g290)
    c: Equal(g293,g294)
    c: Equal(g293,g295)
    c: InternalAlignment(g293,g296)
    c: InternalAlignment(g294,g296)
    c: InternalAlignment(g295,g296)
    c: InternalAlignment(g297,g296)
    c: InternalAlignment(g298,g296)
    c: Block(g284)
    c: Block(g290)
    c: Block(g296)
    c: Block(g278)
    c: Coincident(g299,g278)
    c: Coincident(g299,g284)
    c: Horizontal(g299)
    c: Coincident(g300,g284)
    c: Coincident(g300,g290)
    c: Vertical(g300)
    c: Coincident(g301,g290)
    c: Coincident(g301,g296)
    c: Horizontal(g301)
    c: Coincident(g302,g296)
    c: Coincident(g302,g278)
    c: Weight(g303) = 1
    c: Equal(g303,g304)
    c: Equal(g303,g305)
    c: InternalAlignment(g303,g306)
    c: InternalAlignment(g304,g306)
    c: InternalAlignment(g305,g306)
    c: InternalAlignment(g307,g306)
    c: InternalAlignment(g308,g306)
    c: Weight(g309) = 1
    c: Equal(g309,g310)
    c: Equal(g309,g311)
    c: InternalAlignment(g309,g312)
    c: InternalAlignment(g310,g312)
    c: InternalAlignment(g311,g312)
    c: InternalAlignment(g313,g312)
    c: InternalAlignment(g314,g312)
    c: Weight(g315) = 1
    c: Equal(g315,g316)
    c: Equal(g315,g317)
    c: InternalAlignment(g315,g318)
    c: InternalAlignment(g316,g318)
    c: InternalAlignment(g317,g318)
    c: InternalAlignment(g319,g318)
    c: InternalAlignment(g320,g318)
    c: Block(g318)
    c: Block(g312)
    c: Block(g306)
    c: Coincident(g321,g318)
    c: Coincident(g321,g312)
    c: Horizontal(g321)
    c: Coincident(g322,g312)
    c: Coincident(g322,g306)
    c: Vertical(g322)
    c: Coincident(g323,g306)
    c: Coincident(g323,g318)
    c: InternalAlignment(g324,g325)
    c: InternalAlignment(g326,g325)
    c: InternalAlignment(g327,g325)
    c: Block(g325)
    c: Equal(g328,g329)
    c: Equal(g328,g330)
    c: InternalAlignment(g328,g331)
    c: InternalAlignment(g329,g331)
    c: InternalAlignment(g330,g331)
    c: InternalAlignment(g332,g331)
    c: InternalAlignment(g333,g331)
    c: Block(g331)
    c: Coincident(g334,g325)
    c: Horizontal(g334)
    c: Block(g334)
    c: Coincident(g335,g325)
    c: Coincident(g335,g251)
    c: Vertical(g335)
    c: Coincident(g336,g331)
    c: Coincident(g336,g245)
    c: Vertical(g336)
    c: Block(g337)
    c: Block(g2)
    c: Distance(g335) = 119.89
    c: Coincident(g338,g337)
    c: Coincident(g338,g2)
    c: Coincident(g339,g2)
    c: Coincident(g339,g337)
    c: Block(g3)
    c: Block(g340)
    c: Coincident(g341,g340)
    c: Coincident(g341,g3)
    c: Coincident(g342,g340)
    c: Coincident(g342,g3)
    c: Block(g342)
    c: Block(g341)
    c: Weight(g343) = 1
    c: Equal(g343,g344)
    c: Equal(g343,g345)
    c: InternalAlignment(g343,g346)
    c: InternalAlignment(g344,g346)
    c: InternalAlignment(g345,g346)
    c: InternalAlignment(g347,g346)
    c: InternalAlignment(g348,g346)
    c: Weight(g349) = 1
    c: Equal(g349,g350)
    c: Equal(g349,g351)
    c: InternalAlignment(g349,g352)
    c: InternalAlignment(g350,g352)
    c: InternalAlignment(g351,g352)
    c: InternalAlignment(g353,g352)
    c: InternalAlignment(g354,g352)
    c: Weight(g355) = 1
    c: Equal(g355,g356)
    c: Equal(g355,g357)
    c: InternalAlignment(g355,g358)
    c: InternalAlignment(g356,g358)
    c: InternalAlignment(g357,g358)
    c: InternalAlignment(g359,g358)
    c: InternalAlignment(g360,g358)
    c: Weight(g361) = 1
    c: Equal(g361,g362)
    c: Equal(g361,g363)
    c: InternalAlignment(g361,g364)
    c: InternalAlignment(g362,g364)
    c: InternalAlignment(g363,g364)
    c: InternalAlignment(g365,g364)
    c: InternalAlignment(g366,g364)
    c: Block(g364)
    c: Block(g358)
    c: Block(g352)
    c: Block(g346)
    c: Coincident(g367,g364)
    c: Coincident(g367,g346)
    c: Vertical(g367)
    c: Coincident(g368,g346)
    c: Coincident(g368,g352)
    c: Coincident(g369,g352)
    c: Coincident(g369,g358)
    c: Vertical(g369)
    c: Coincident(g370,g358)
    c: Coincident(g370,g364)
    c: Horizontal(g370)
    c: Vertical(g371)
    c: Vertical(g372)
    c: Vertical(g373)
    c: Vertical(g374)
    c: Coincident(g375,g0)
    c: Coincident(g375,g1)
    c: Horizontal(g375)
    c: Block(g375)
    c: Distance(g375) = 450
    c: Block(g373)
    c: Block(g371)
    c: Block(g372)
    c: Block(g374)
    c: Distance(g0) = 240
    c: Horizontal(g376)
    c: Distance(g376) = 12
    c: Coincident(g376,g371)
    c: Vertical(g377)
    c: Distance(g377) = 12
    c: Coincident(g377,g371)
    c: Coincident(g378,g376)
    c: Vertical(g378)
    c: Horizontal(g379)
    c: Vertical(g380)
    c: Distance(g380) = 6
    c: Coincident(g380,g376)
    c: Coincident(g379,g376)
    c: Block(g378)
    c: Coincident(g381,g378)
    c: Horizontal(g381)
    c: Distance(g381) = 6
    c: Vertical(g382)
    c: Distance(g382) = 3
    c: Vertical(g383)
    c: Distance(g383) = 3
    c: Coincident(g383,g371)
    c: Coincident(g377,g382)
    c: Coincident(g389,g383)
    c: Weight(g384) = 1
    c: Equal(g384,g385)
    c: Coincident(g385,g379)
    c: Equal(g384,g386)
    c: Coincident(g386,g380)
    c: Equal(g384,g387)
    c: Coincident(g387,g381)
    c: Equal(g384,g388)
    c: Coincident(g389,g382)
    c: InternalAlignment(g384-g388 -> g389) x5
    c: InternalAlignment(g390,g389)
    c: InternalAlignment(g391,g389)
    c: InternalAlignment(g392,g389)
    c: Coincident(g393,g164)
    c: Coincident(g393,g158)
    c: Horizontal(g393)
    c: Block(g389)
    c: Horizontal(g394)
FEATURE [Part::Extrusion] Extrude005
  Base = -> Sketch003
  Dir = (0,0,1)
  DirMode = 2
  FaceMakerClass = Part::FaceMakerBullseye
  LengthFwd = 24
  LengthRev = 0
  Solid = true
  Symmetric = false
